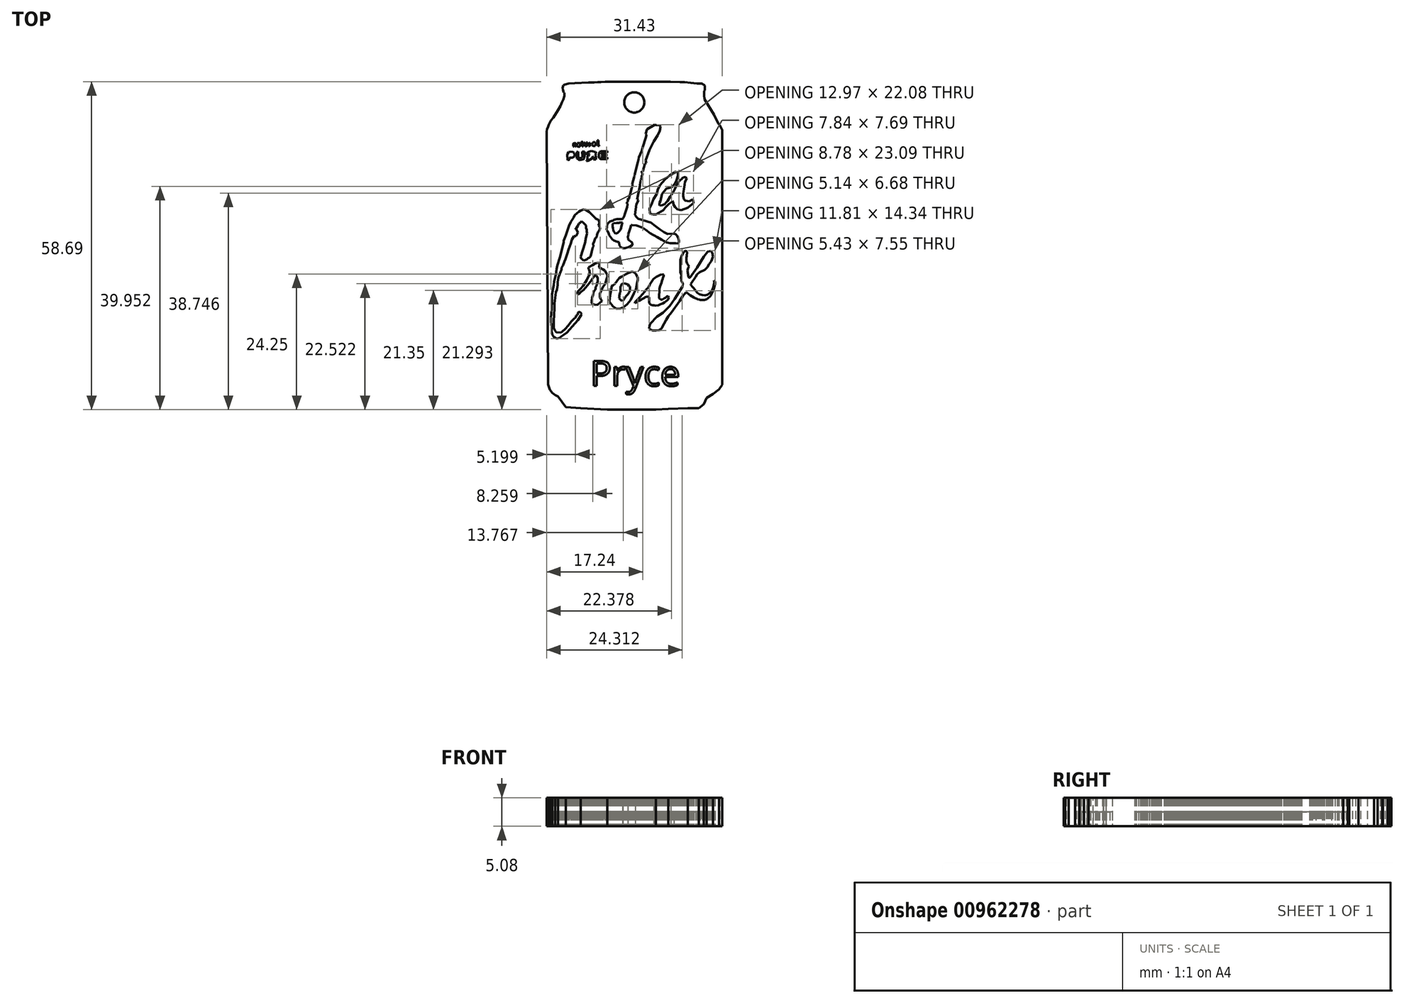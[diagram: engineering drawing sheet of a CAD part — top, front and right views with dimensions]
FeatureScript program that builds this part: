
annotation { "Feature Type Name" : "Feature", "Feature Type Description" : "" }
export const myFeature = defineFeature(function(context is Context, id is Id, definition is map)
    precondition{}
    {
        {
            var Q0;
            Q0=qCreatedBy(makeId("Top.planeOp"),FACE);
            var sketch = newSketch(context, id + "F0", { "sketchPlane" : qUnion([Q0])});
            skLineSegment(sketch, "E0", {"start": v(-26.3, 34.2) * mm, "end": v(-26, -11.02) * mm});
            skLineSegment(sketch, "E1", {"start": v(-26, -11.02) * mm, "end": v(-25.72, -12.03) * mm});
            skLineSegment(sketch, "E2", {"start": v(-25.72, -12.03) * mm, "end": v(-25.25, -12.55) * mm});
            skLineSegment(sketch, "E3", {"start": v(-25.25, -12.55) * mm, "end": v(-24.77, -12.95) * mm});
            skLineSegment(sketch, "E4", {"start": v(-24.77, -12.95) * mm, "end": v(-24.25, -13.22) * mm});
            skLineSegment(sketch, "E5", {"start": v(-24.25, -13.22) * mm, "end": v(-22.83, -15.1) * mm});
            skLineSegment(sketch, "E6", {"start": v(-22.83, -15.1) * mm, "end": v(-20.16, -15.3) * mm});
            skLineSegment(sketch, "E7", {"start": v(-20.16, -15.3) * mm, "end": v(-17.96, -15.41) * mm});
            skLineSegment(sketch, "E8", {"start": v(-17.96, -15.41) * mm, "end": v(-15.42, -15.55) * mm});
            skLineSegment(sketch, "E9", {"start": v(-15.42, -15.55) * mm, "end": v(-12.93, -15.55) * mm});
            skLineSegment(sketch, "E10", {"start": v(-12.93, -15.55) * mm, "end": v(-10.85, -15.55) * mm});
            skLineSegment(sketch, "E11", {"start": v(-10.85, -15.55) * mm, "end": v(-9.02, -15.55) * mm});
            skLineSegment(sketch, "E12", {"start": v(-9.02, -15.55) * mm, "end": v(-6.74, -15.55) * mm});
            skLineSegment(sketch, "E13", {"start": v(-6.74, -15.55) * mm, "end": v(-4.52, -15.41) * mm});
            skLineSegment(sketch, "E14", {"start": v(-4.52, -15.41) * mm, "end": v(-1, -15.27) * mm});
            skLineSegment(sketch, "E15", {"start": v(-1, -15.27) * mm, "end": v(0.95, -15.27) * mm});
            skLineSegment(sketch, "E16", {"start": v(0.95, -15.27) * mm, "end": v(1.88, -14.61) * mm});
            skLineSegment(sketch, "E17", {"start": v(1.88, -14.61) * mm, "end": v(2.35, -13.48) * mm});
            skLineSegment(sketch, "E18", {"start": v(2.35, -13.48) * mm, "end": v(3.5, -12.76) * mm});
            skLineSegment(sketch, "E19", {"start": v(3.5, -12.76) * mm, "end": v(4.6, -11.91) * mm});
            skLineSegment(sketch, "E20", {"start": v(4.6, -11.91) * mm, "end": v(5.13, -11.11) * mm});
            skLineSegment(sketch, "E21", {"start": v(5.13, -11.11) * mm, "end": v(5.13, -10.3) * mm});
            skLineSegment(sketch, "E22", {"start": v(5.13, -10.3) * mm, "end": v(5.13, -6.08) * mm});
            skLineSegment(sketch, "E23", {"start": v(5.13, -6.08) * mm, "end": v(5.13, -5.6) * mm});
            skLineSegment(sketch, "E24", {"start": v(5.13, -5.6) * mm, "end": v(5.13, 0.5) * mm});
            skLineSegment(sketch, "E25", {"start": v(5.13, 0.5) * mm, "end": v(5.13, 34.49) * mm});
            skLineSegment(sketch, "E26", {"start": v(5.13, 34.49) * mm, "end": v(4.7, 35.36) * mm});
            skLineSegment(sketch, "E27", {"start": v(4.7, 35.36) * mm, "end": v(4.48, 35.62) * mm});
            skLineSegment(sketch, "E28", {"start": v(4.48, 35.62) * mm, "end": v(3.68, 37.23) * mm});
            skLineSegment(sketch, "E29", {"start": v(3.68, 37.23) * mm, "end": v(3.07, 38.24) * mm});
            skLineSegment(sketch, "E30", {"start": v(3.07, 38.24) * mm, "end": v(2, 40.03) * mm});
            skLineSegment(sketch, "E31", {"start": v(2, 40.03) * mm, "end": v(1.9, 40.69) * mm});
            skLineSegment(sketch, "E32", {"start": v(1.9, 40.69) * mm, "end": v(1.9, 41.12) * mm});
            skLineSegment(sketch, "E33", {"start": v(1.9, 41.12) * mm, "end": v(1.9, 41.46) * mm});
            skLineSegment(sketch, "E34", {"start": v(1.9, 41.46) * mm, "end": v(2.07, 41.6) * mm});
            skLineSegment(sketch, "E35", {"start": v(2.07, 41.6) * mm, "end": v(2.07, 41.93) * mm});
            skLineSegment(sketch, "E36", {"start": v(2.07, 41.93) * mm, "end": v(2.07, 42.42) * mm});
            skLineSegment(sketch, "E37", {"start": v(2.07, 42.42) * mm, "end": v(1.95, 42.56) * mm});
            skLineSegment(sketch, "E38", {"start": v(1.95, 42.56) * mm, "end": v(1.49, 42.8) * mm});
            skLineSegment(sketch, "E39", {"start": v(1.49, 42.8) * mm, "end": v(0.65, 42.8) * mm});
            skLineSegment(sketch, "E40", {"start": v(0.65, 42.8) * mm, "end": v(-0.46, 42.95) * mm});
            skLineSegment(sketch, "E41", {"start": v(-0.46, 42.95) * mm, "end": v(-1.54, 43.05) * mm});
            skLineSegment(sketch, "E42", {"start": v(-1.54, 43.05) * mm, "end": v(-2.4, 43.05) * mm});
            skLineSegment(sketch, "E43", {"start": v(-2.4, 43.05) * mm, "end": v(-4.13, 43.14) * mm});
            skLineSegment(sketch, "E44", {"start": v(-4.13, 43.14) * mm, "end": v(-5.15, 43.14) * mm});
            skLineSegment(sketch, "E45", {"start": v(-5.15, 43.14) * mm, "end": v(-6.54, 43.14) * mm});
            skLineSegment(sketch, "E46", {"start": v(-6.54, 43.14) * mm, "end": v(-8.61, 43.14) * mm});
            skLineSegment(sketch, "E47", {"start": v(-8.61, 43.14) * mm, "end": v(-9.4, 43.14) * mm});
            skLineSegment(sketch, "E48", {"start": v(-9.4, 43.14) * mm, "end": v(-10.07, 43.14) * mm});
            skLineSegment(sketch, "E49", {"start": v(-10.07, 43.14) * mm, "end": v(-11.08, 43.14) * mm});
            skLineSegment(sketch, "E50", {"start": v(-11.08, 43.14) * mm, "end": v(-13.23, 43.14) * mm});
            skLineSegment(sketch, "E51", {"start": v(-13.23, 43.14) * mm, "end": v(-14.73, 43.14) * mm});
            skLineSegment(sketch, "E52", {"start": v(-14.73, 43.14) * mm, "end": v(-15.8, 43.14) * mm});
            skLineSegment(sketch, "E53", {"start": v(-15.8, 43.14) * mm, "end": v(-16.56, 43.05) * mm});
            skLineSegment(sketch, "E54", {"start": v(-16.56, 43.05) * mm, "end": v(-17.14, 43.05) * mm});
            skLineSegment(sketch, "E55", {"start": v(-17.14, 43.05) * mm, "end": v(-17.78, 42.99) * mm});
            skLineSegment(sketch, "E56", {"start": v(-17.78, 42.99) * mm, "end": v(-18.77, 42.99) * mm});
            skLineSegment(sketch, "E57", {"start": v(-18.77, 42.99) * mm, "end": v(-20.2, 42.93) * mm});
            skLineSegment(sketch, "E58", {"start": v(-20.2, 42.93) * mm, "end": v(-21.23, 42.88) * mm});
            skLineSegment(sketch, "E59", {"start": v(-21.23, 42.88) * mm, "end": v(-22.32, 42.8) * mm});
            skLineSegment(sketch, "E60", {"start": v(-22.32, 42.8) * mm, "end": v(-23.06, 42.6) * mm});
            skLineSegment(sketch, "E61", {"start": v(-23.06, 42.6) * mm, "end": v(-23.3, 42.46) * mm});
            skLineSegment(sketch, "E62", {"start": v(-23.3, 42.46) * mm, "end": v(-23.4, 42.01) * mm});
            skLineSegment(sketch, "E63", {"start": v(-23.4, 42.01) * mm, "end": v(-23.38, 41.66) * mm});
            skLineSegment(sketch, "E64", {"start": v(-23.38, 41.66) * mm, "end": v(-23.2, 41.21) * mm});
            skLineSegment(sketch, "E65", {"start": v(-23.2, 41.21) * mm, "end": v(-23.12, 41.12) * mm});
            skLineSegment(sketch, "E66", {"start": v(-23.12, 41.12) * mm, "end": v(-23.12, 40.57) * mm});
            skLineSegment(sketch, "E67", {"start": v(-23.12, 40.57) * mm, "end": v(-23.3, 39.97) * mm});
            skLineSegment(sketch, "E68", {"start": v(-23.3, 39.97) * mm, "end": v(-23.54, 39.42) * mm});
            skLineSegment(sketch, "E69", {"start": v(-23.54, 39.42) * mm, "end": v(-23.8, 38.82) * mm});
            skLineSegment(sketch, "E70", {"start": v(-23.8, 38.82) * mm, "end": v(-24.26, 38.06) * mm});
            skLineSegment(sketch, "E71", {"start": v(-24.26, 38.06) * mm, "end": v(-24.64, 37.44) * mm});
            skLineSegment(sketch, "E72", {"start": v(-24.64, 37.44) * mm, "end": v(-25.09, 36.7) * mm});
            skLineSegment(sketch, "E73", {"start": v(-25.09, 36.7) * mm, "end": v(-25.5, 36.19) * mm});
            skLineSegment(sketch, "E74", {"start": v(-25.5, 36.19) * mm, "end": v(-25.88, 35.44) * mm});
            skLineSegment(sketch, "E75", {"start": v(-25.88, 35.44) * mm, "end": v(-26.04, 35.02) * mm});
            skLineSegment(sketch, "E76", {"start": v(-26.04, 35.02) * mm, "end": v(-26.18, 34.6) * mm});
            skLineSegment(sketch, "E77", {"start": v(-26.18, 34.6) * mm, "end": v(-26.3, 34.2) * mm});
            skLineSegment(sketch, "E78", {"start": v(-8.56, 33.78) * mm, "end": v(-8.31, 34.6) * mm});
            skLineSegment(sketch, "E79", {"start": v(-8.31, 34.6) * mm, "end": v(-6.9, 35.44) * mm});
            skLineSegment(sketch, "E80", {"start": v(-6.9, 35.44) * mm, "end": v(-6.71, 35.38) * mm});
            skLineSegment(sketch, "E81", {"start": v(-6.71, 35.38) * mm, "end": v(-6.17, 35.32) * mm});
            skLineSegment(sketch, "E82", {"start": v(-6.17, 35.32) * mm, "end": v(-6.04, 35.32) * mm});
            skLineSegment(sketch, "E83", {"start": v(-6.04, 35.32) * mm, "end": v(-5.88, 35.05) * mm});
            skLineSegment(sketch, "E84", {"start": v(-5.88, 35.05) * mm, "end": v(-6, 34.33) * mm});
            skLineSegment(sketch, "E85", {"start": v(-6, 34.33) * mm, "end": v(-6.2, 33.97) * mm});
            skLineSegment(sketch, "E86", {"start": v(-6.2, 33.97) * mm, "end": v(-6.4, 33.55) * mm});
            skLineSegment(sketch, "E87", {"start": v(-6.4, 33.55) * mm, "end": v(-7.09, 32.44) * mm});
            skLineSegment(sketch, "E88", {"start": v(-7.09, 32.44) * mm, "end": v(-7.84, 30.96) * mm});
            skLineSegment(sketch, "E89", {"start": v(-7.84, 30.96) * mm, "end": v(-8.54, 29) * mm});
            skLineSegment(sketch, "E90", {"start": v(-8.54, 29) * mm, "end": v(-8.44, 28.6) * mm});
            skLineSegment(sketch, "E91", {"start": v(-8.44, 28.6) * mm, "end": v(-8.66, 28.48) * mm});
            skLineSegment(sketch, "E92", {"start": v(-8.66, 28.48) * mm, "end": v(-9.1, 27.04) * mm});
            skLineSegment(sketch, "E93", {"start": v(-9.1, 27.04) * mm, "end": v(-9.26, 27.1) * mm});
            skLineSegment(sketch, "E94", {"start": v(-9.26, 27.1) * mm, "end": v(-9.26, 26.85) * mm});
            skLineSegment(sketch, "E95", {"start": v(-9.26, 26.85) * mm, "end": v(-9.1, 26.7) * mm});
            skLineSegment(sketch, "E96", {"start": v(-9.1, 26.7) * mm, "end": v(-9.17, 26.27) * mm});
            skLineSegment(sketch, "E97", {"start": v(-9.17, 26.27) * mm, "end": v(-9.28, 26.17) * mm});
            skLineSegment(sketch, "E98", {"start": v(-9.28, 26.17) * mm, "end": v(-9.38, 26.09) * mm});
            skLineSegment(sketch, "E99", {"start": v(-9.38, 26.09) * mm, "end": v(-9.28, 25.93) * mm});
            skLineSegment(sketch, "E100", {"start": v(-9.28, 25.93) * mm, "end": v(-9.42, 25.66) * mm});
            skLineSegment(sketch, "E101", {"start": v(-9.42, 25.66) * mm, "end": v(-9.41, 25.44) * mm});
            skLineSegment(sketch, "E102", {"start": v(-9.41, 25.44) * mm, "end": v(-9.5, 25.26) * mm});
            skLineSegment(sketch, "E103", {"start": v(-9.5, 25.26) * mm, "end": v(-9.58, 24.53) * mm});
            skLineSegment(sketch, "E104", {"start": v(-9.58, 24.53) * mm, "end": v(-10.07, 22) * mm});
            skLineSegment(sketch, "E105", {"start": v(-10.07, 22) * mm, "end": v(-9.85, 21.9) * mm});
            skLineSegment(sketch, "E106", {"start": v(-9.85, 21.9) * mm, "end": v(-10.2, 21.19) * mm});
            skLineSegment(sketch, "E107", {"start": v(-10.2, 21.19) * mm, "end": v(-10.47, 19.31) * mm});
            skLineSegment(sketch, "E108", {"start": v(-10.47, 19.31) * mm, "end": v(-10.23, 18.91) * mm});
            skLineSegment(sketch, "E109", {"start": v(-10.23, 18.91) * mm, "end": v(-9.88, 18.6) * mm});
            skLineSegment(sketch, "E110", {"start": v(-9.88, 18.6) * mm, "end": v(-8.89, 18.3) * mm});
            skLineSegment(sketch, "E111", {"start": v(-8.89, 18.3) * mm, "end": v(-7.6, 17.92) * mm});
            skLineSegment(sketch, "E112", {"start": v(-7.6, 17.92) * mm, "end": v(-6.76, 17.27) * mm});
            skLineSegment(sketch, "E113", {"start": v(-6.76, 17.27) * mm, "end": v(-6.05, 16.68) * mm});
            skLineSegment(sketch, "E114", {"start": v(-6.05, 16.68) * mm, "end": v(-5.26, 16.2) * mm});
            skLineSegment(sketch, "E115", {"start": v(-5.26, 16.2) * mm, "end": v(-4.62, 15.88) * mm});
            skLineSegment(sketch, "E116", {"start": v(-4.62, 15.88) * mm, "end": v(-3.46, 15.93) * mm});
            skLineSegment(sketch, "E117", {"start": v(-3.46, 15.93) * mm, "end": v(-3.15, 15.84) * mm});
            skLineSegment(sketch, "E118", {"start": v(-3.15, 15.84) * mm, "end": v(-2.98, 15.64) * mm});
            skLineSegment(sketch, "E119", {"start": v(-2.98, 15.64) * mm, "end": v(-2.71, 15.19) * mm});
            skLineSegment(sketch, "E120", {"start": v(-2.71, 15.19) * mm, "end": v(-2.58, 14.7) * mm});
            skLineSegment(sketch, "E121", {"start": v(-2.58, 14.7) * mm, "end": v(-2.58, 14.35) * mm});
            skLineSegment(sketch, "E122", {"start": v(-2.58, 14.35) * mm, "end": v(-2.8, 14.17) * mm});
            skLineSegment(sketch, "E123", {"start": v(-2.8, 14.17) * mm, "end": v(-3.17, 14.22) * mm});
            skLineSegment(sketch, "E124", {"start": v(-3.17, 14.22) * mm, "end": v(-4.17, 14.22) * mm});
            skLineSegment(sketch, "E125", {"start": v(-4.17, 14.22) * mm, "end": v(-4.73, 14.37) * mm});
            skLineSegment(sketch, "E126", {"start": v(-4.73, 14.37) * mm, "end": v(-5.24, 14.58) * mm});
            skLineSegment(sketch, "E127", {"start": v(-5.24, 14.58) * mm, "end": v(-5.73, 14.88) * mm});
            skLineSegment(sketch, "E128", {"start": v(-5.73, 14.88) * mm, "end": v(-6.46, 15.32) * mm});
            skLineSegment(sketch, "E129", {"start": v(-6.46, 15.32) * mm, "end": v(-7.75, 15.99) * mm});
            skLineSegment(sketch, "E130", {"start": v(-7.75, 15.99) * mm, "end": v(-8.59, 16.62) * mm});
            skLineSegment(sketch, "E131", {"start": v(-8.59, 16.62) * mm, "end": v(-9.13, 17) * mm});
            skLineSegment(sketch, "E132", {"start": v(-9.13, 17) * mm, "end": v(-10.21, 17.38) * mm});
            skLineSegment(sketch, "E133", {"start": v(-10.21, 17.38) * mm, "end": v(-11, 17.46) * mm});
            skLineSegment(sketch, "E134", {"start": v(-11, 17.46) * mm, "end": v(-11.19, 17.46) * mm});
            skLineSegment(sketch, "E135", {"start": v(-11.19, 17.46) * mm, "end": v(-11.24, 17.12) * mm});
            skLineSegment(sketch, "E136", {"start": v(-11.24, 17.12) * mm, "end": v(-11.52, 16.2) * mm});
            skLineSegment(sketch, "E137", {"start": v(-11.52, 16.2) * mm, "end": v(-11.7, 15.86) * mm});
            skLineSegment(sketch, "E138", {"start": v(-11.7, 15.86) * mm, "end": v(-11.6, 15.68) * mm});
            skLineSegment(sketch, "E139", {"start": v(-11.6, 15.68) * mm, "end": v(-11.74, 15.46) * mm});
            skLineSegment(sketch, "E140", {"start": v(-11.74, 15.46) * mm, "end": v(-11.68, 14.86) * mm});
            skLineSegment(sketch, "E141", {"start": v(-11.68, 14.86) * mm, "end": v(-11, 14.37) * mm});
            skLineSegment(sketch, "E142", {"start": v(-11, 14.37) * mm, "end": v(-10.89, 13.9) * mm});
            skLineSegment(sketch, "E143", {"start": v(-10.89, 13.9) * mm, "end": v(-11.42, 13.57) * mm});
            skLineSegment(sketch, "E144", {"start": v(-11.42, 13.57) * mm, "end": v(-12.25, 13.36) * mm});
            skLineSegment(sketch, "E145", {"start": v(-12.25, 13.36) * mm, "end": v(-12.65, 13.36) * mm});
            skLineSegment(sketch, "E146", {"start": v(-12.65, 13.36) * mm, "end": v(-13.06, 13.57) * mm});
            skLineSegment(sketch, "E147", {"start": v(-13.06, 13.57) * mm, "end": v(-13.23, 13.86) * mm});
            skLineSegment(sketch, "E148", {"start": v(-13.23, 13.86) * mm, "end": v(-13.34, 14.43) * mm});
            skLineSegment(sketch, "E149", {"start": v(-13.34, 14.43) * mm, "end": v(-13.8, 14.57) * mm});
            skLineSegment(sketch, "E150", {"start": v(-13.8, 14.57) * mm, "end": v(-14.25, 14.75) * mm});
            skLineSegment(sketch, "E151", {"start": v(-14.25, 14.75) * mm, "end": v(-14.5, 14.93) * mm});
            skLineSegment(sketch, "E152", {"start": v(-14.5, 14.93) * mm, "end": v(-15.08, 15.7) * mm});
            skLineSegment(sketch, "E153", {"start": v(-15.08, 15.7) * mm, "end": v(-15.13, 15.98) * mm});
            skLineSegment(sketch, "E154", {"start": v(-15.13, 15.98) * mm, "end": v(-15.4, 16.43) * mm});
            skLineSegment(sketch, "E155", {"start": v(-15.4, 16.43) * mm, "end": v(-15.54, 16.6) * mm});
            skLineSegment(sketch, "E156", {"start": v(-15.54, 16.6) * mm, "end": v(-15.49, 17.15) * mm});
            skLineSegment(sketch, "E157", {"start": v(-15.49, 17.15) * mm, "end": v(-15.4, 17.64) * mm});
            skLineSegment(sketch, "E158", {"start": v(-15.4, 17.64) * mm, "end": v(-14.99, 18.07) * mm});
            skLineSegment(sketch, "E159", {"start": v(-14.99, 18.07) * mm, "end": v(-14.61, 18.25) * mm});
            skLineSegment(sketch, "E160", {"start": v(-14.61, 18.25) * mm, "end": v(-14.41, 18.25) * mm});
            skLineSegment(sketch, "E161", {"start": v(-14.41, 18.25) * mm, "end": v(-14.22, 18.42) * mm});
            skLineSegment(sketch, "E162", {"start": v(-14.22, 18.42) * mm, "end": v(-13.67, 18.52) * mm});
            skLineSegment(sketch, "E163", {"start": v(-13.67, 18.52) * mm, "end": v(-13.22, 18.55) * mm});
            skLineSegment(sketch, "E164", {"start": v(-13.22, 18.55) * mm, "end": v(-12.9, 18.54) * mm});
            skLineSegment(sketch, "E165", {"start": v(-12.9, 18.54) * mm, "end": v(-12.71, 18.54) * mm});
            skLineSegment(sketch, "E166", {"start": v(-12.71, 18.54) * mm, "end": v(-12.54, 18.71) * mm});
            skLineSegment(sketch, "E167", {"start": v(-12.54, 18.71) * mm, "end": v(-12.46, 18.87) * mm});
            skLineSegment(sketch, "E168", {"start": v(-12.46, 18.87) * mm, "end": v(-12.34, 19.12) * mm});
            skLineSegment(sketch, "E169", {"start": v(-12.34, 19.12) * mm, "end": v(-12.27, 19.39) * mm});
            skLineSegment(sketch, "E170", {"start": v(-12.27, 19.39) * mm, "end": v(-11.87, 20.73) * mm});
            skLineSegment(sketch, "E171", {"start": v(-11.87, 20.73) * mm, "end": v(-11.78, 21.13) * mm});
            skLineSegment(sketch, "E172", {"start": v(-11.78, 21.13) * mm, "end": v(-11.8, 21.25) * mm});
            skLineSegment(sketch, "E173", {"start": v(-11.8, 21.25) * mm, "end": v(-11.92, 21.27) * mm});
            skLineSegment(sketch, "E174", {"start": v(-11.92, 21.27) * mm, "end": v(-11.84, 21.57) * mm});
            skLineSegment(sketch, "E175", {"start": v(-11.84, 21.57) * mm, "end": v(-11.71, 21.67) * mm});
            skLineSegment(sketch, "E176", {"start": v(-11.71, 21.67) * mm, "end": v(-11.73, 21.81) * mm});
            skLineSegment(sketch, "E177", {"start": v(-11.73, 21.81) * mm, "end": v(-11.84, 21.94) * mm});
            skLineSegment(sketch, "E178", {"start": v(-11.84, 21.94) * mm, "end": v(-11.55, 22.17) * mm});
            skLineSegment(sketch, "E179", {"start": v(-11.55, 22.17) * mm, "end": v(-11.47, 22.45) * mm});
            skLineSegment(sketch, "E180", {"start": v(-11.47, 22.45) * mm, "end": v(-11.4, 22.74) * mm});
            skLineSegment(sketch, "E181", {"start": v(-11.4, 22.74) * mm, "end": v(-11.33, 22.93) * mm});
            skLineSegment(sketch, "E182", {"start": v(-11.33, 22.93) * mm, "end": v(-11.3, 23.18) * mm});
            skLineSegment(sketch, "E183", {"start": v(-11.3, 23.18) * mm, "end": v(-11.19, 23.64) * mm});
            skLineSegment(sketch, "E184", {"start": v(-11.19, 23.64) * mm, "end": v(-11.06, 24.12) * mm});
            skLineSegment(sketch, "E185", {"start": v(-11.06, 24.12) * mm, "end": v(-10.9, 24.3) * mm});
            skLineSegment(sketch, "E186", {"start": v(-10.9, 24.3) * mm, "end": v(-10.91, 24.62) * mm});
            skLineSegment(sketch, "E187", {"start": v(-10.91, 24.62) * mm, "end": v(-10.96, 24.76) * mm});
            skLineSegment(sketch, "E188", {"start": v(-10.96, 24.76) * mm, "end": v(-10.88, 25.05) * mm});
            skLineSegment(sketch, "E189", {"start": v(-10.88, 25.05) * mm, "end": v(-10.77, 25.5) * mm});
            skLineSegment(sketch, "E190", {"start": v(-10.77, 25.5) * mm, "end": v(-10.64, 25.93) * mm});
            skLineSegment(sketch, "E191", {"start": v(-10.64, 25.93) * mm, "end": v(-10.58, 26.12) * mm});
            skLineSegment(sketch, "E192", {"start": v(-10.58, 26.12) * mm, "end": v(-10.65, 26.23) * mm});
            skLineSegment(sketch, "E193", {"start": v(-10.65, 26.23) * mm, "end": v(-10.5, 26.37) * mm});
            skLineSegment(sketch, "E194", {"start": v(-10.5, 26.37) * mm, "end": v(-10.5, 26.49) * mm});
            skLineSegment(sketch, "E195", {"start": v(-10.5, 26.49) * mm, "end": v(-10.19, 27.69) * mm});
            skLineSegment(sketch, "E196", {"start": v(-10.19, 27.69) * mm, "end": v(-9.93, 28.71) * mm});
            skLineSegment(sketch, "E197", {"start": v(-9.93, 28.71) * mm, "end": v(-9.82, 29.22) * mm});
            skLineSegment(sketch, "E198", {"start": v(-9.82, 29.22) * mm, "end": v(-9.74, 29.6) * mm});
            skLineSegment(sketch, "E199", {"start": v(-9.74, 29.6) * mm, "end": v(-9.28, 30.74) * mm});
            skLineSegment(sketch, "E200", {"start": v(-9.28, 30.74) * mm, "end": v(-9.14, 31.15) * mm});
            skLineSegment(sketch, "E201", {"start": v(-9.14, 31.15) * mm, "end": v(-9.05, 31.45) * mm});
            skLineSegment(sketch, "E202", {"start": v(-9.05, 31.45) * mm, "end": v(-8.57, 33.03) * mm});
            skLineSegment(sketch, "E203", {"start": v(-8.57, 33.03) * mm, "end": v(-8.46, 33.46) * mm});
            skLineSegment(sketch, "E204", {"start": v(-8.46, 33.46) * mm, "end": v(-8.46, 33.64) * mm});
            skLineSegment(sketch, "E205", {"start": v(-8.46, 33.64) * mm, "end": v(-8.56, 33.78) * mm});
            skLineSegment(sketch, "E206", {"start": v(-14.22, 16.25) * mm, "end": v(-14.02, 16) * mm});
            skLineSegment(sketch, "E207", {"start": v(-14.02, 16) * mm, "end": v(-13.93, 15.96) * mm});
            skLineSegment(sketch, "E208", {"start": v(-13.93, 15.96) * mm, "end": v(-13.74, 16.02) * mm});
            skLineSegment(sketch, "E209", {"start": v(-13.74, 16.02) * mm, "end": v(-13.58, 16.1) * mm});
            skLineSegment(sketch, "E210", {"start": v(-13.58, 16.1) * mm, "end": v(-13.3, 16.3) * mm});
            skLineSegment(sketch, "E211", {"start": v(-13.3, 16.3) * mm, "end": v(-13, 16.7) * mm});
            skLineSegment(sketch, "E212", {"start": v(-13, 16.7) * mm, "end": v(-12.85, 17.3) * mm});
            skLineSegment(sketch, "E213", {"start": v(-12.85, 17.3) * mm, "end": v(-12.76, 17.79) * mm});
            skLineSegment(sketch, "E214", {"start": v(-12.76, 17.79) * mm, "end": v(-12.77, 17.89) * mm});
            skLineSegment(sketch, "E215", {"start": v(-12.77, 17.89) * mm, "end": v(-13.04, 17.96) * mm});
            skLineSegment(sketch, "E216", {"start": v(-13.04, 17.96) * mm, "end": v(-13.3, 17.86) * mm});
            skLineSegment(sketch, "E217", {"start": v(-13.3, 17.86) * mm, "end": v(-13.77, 17.82) * mm});
            skLineSegment(sketch, "E218", {"start": v(-13.77, 17.82) * mm, "end": v(-14.25, 17.76) * mm});
            skLineSegment(sketch, "E219", {"start": v(-14.25, 17.76) * mm, "end": v(-14.48, 17.67) * mm});
            skLineSegment(sketch, "E220", {"start": v(-14.48, 17.67) * mm, "end": v(-14.46, 17.24) * mm});
            skLineSegment(sketch, "E221", {"start": v(-14.46, 17.24) * mm, "end": v(-14.38, 16.86) * mm});
            skLineSegment(sketch, "E222", {"start": v(-14.38, 16.86) * mm, "end": v(-14.3, 16.5) * mm});
            skLineSegment(sketch, "E223", {"start": v(-14.3, 16.5) * mm, "end": v(-14.22, 16.25) * mm});
            skLineSegment(sketch, "E224", {"start": v(-3.1, 27.04) * mm, "end": v(-4.22, 26.37) * mm});
            skLineSegment(sketch, "E225", {"start": v(-4.22, 26.37) * mm, "end": v(-5.15, 25.6) * mm});
            skLineSegment(sketch, "E226", {"start": v(-5.15, 25.6) * mm, "end": v(-5.96, 24.64) * mm});
            skLineSegment(sketch, "E227", {"start": v(-5.96, 24.64) * mm, "end": v(-6.32, 23.94) * mm});
            skLineSegment(sketch, "E228", {"start": v(-6.32, 23.94) * mm, "end": v(-6.6, 23) * mm});
            skLineSegment(sketch, "E229", {"start": v(-6.6, 23) * mm, "end": v(-7.16, 22.1) * mm});
            skLineSegment(sketch, "E230", {"start": v(-7.16, 22.1) * mm, "end": v(-7.47, 21.19) * mm});
            skLineSegment(sketch, "E231", {"start": v(-7.47, 21.19) * mm, "end": v(-7.84, 20.47) * mm});
            skLineSegment(sketch, "E232", {"start": v(-7.84, 20.47) * mm, "end": v(-7.8, 19.58) * mm});
            skLineSegment(sketch, "E233", {"start": v(-7.8, 19.58) * mm, "end": v(-7.5, 19.4) * mm});
            skLineSegment(sketch, "E234", {"start": v(-7.5, 19.4) * mm, "end": v(-7.17, 19.35) * mm});
            skLineSegment(sketch, "E235", {"start": v(-7.17, 19.35) * mm, "end": v(-6.7, 19.36) * mm});
            skLineSegment(sketch, "E236", {"start": v(-6.7, 19.36) * mm, "end": v(-5.37, 20.15) * mm});
            skLineSegment(sketch, "E237", {"start": v(-5.37, 20.15) * mm, "end": v(-4.97, 20.63) * mm});
            skLineSegment(sketch, "E238", {"start": v(-4.97, 20.63) * mm, "end": v(-4.38, 21.3) * mm});
            skLineSegment(sketch, "E239", {"start": v(-4.38, 21.3) * mm, "end": v(-3.82, 21.68) * mm});
            skLineSegment(sketch, "E240", {"start": v(-3.82, 21.68) * mm, "end": v(-3.75, 21.8) * mm});
            skLineSegment(sketch, "E241", {"start": v(-3.75, 21.8) * mm, "end": v(-3.6, 21.6) * mm});
            skLineSegment(sketch, "E242", {"start": v(-3.6, 21.6) * mm, "end": v(-3.6, 21.21) * mm});
            skLineSegment(sketch, "E243", {"start": v(-3.6, 21.21) * mm, "end": v(-3.3, 20.7) * mm});
            skLineSegment(sketch, "E244", {"start": v(-3.3, 20.7) * mm, "end": v(-2.9, 20.3) * mm});
            skLineSegment(sketch, "E245", {"start": v(-2.9, 20.3) * mm, "end": v(-2.2, 20.14) * mm});
            skLineSegment(sketch, "E246", {"start": v(-2.2, 20.14) * mm, "end": v(-1, 20.56) * mm});
            skLineSegment(sketch, "E247", {"start": v(-1, 20.56) * mm, "end": v(-0.38, 21.08) * mm});
            skLineSegment(sketch, "E248", {"start": v(-0.38, 21.08) * mm, "end": v(0, 21.39) * mm});
            skLineSegment(sketch, "E249", {"start": v(0, 21.39) * mm, "end": v(-0.03, 21.98) * mm});
            skLineSegment(sketch, "E250", {"start": v(-0.03, 21.98) * mm, "end": v(-0.2, 22.03) * mm});
            skLineSegment(sketch, "E251", {"start": v(-0.2, 22.03) * mm, "end": v(-0.73, 21.72) * mm});
            skLineSegment(sketch, "E252", {"start": v(-0.73, 21.72) * mm, "end": v(-1.46, 21.85) * mm});
            skLineSegment(sketch, "E253", {"start": v(-1.46, 21.85) * mm, "end": v(-1.72, 22.07) * mm});
            skLineSegment(sketch, "E254", {"start": v(-1.72, 22.07) * mm, "end": v(-1.77, 22.37) * mm});
            skLineSegment(sketch, "E255", {"start": v(-1.77, 22.37) * mm, "end": v(-1.84, 22.67) * mm});
            skLineSegment(sketch, "E256", {"start": v(-1.84, 22.67) * mm, "end": v(-1.8, 23.15) * mm});
            skLineSegment(sketch, "E257", {"start": v(-1.8, 23.15) * mm, "end": v(-1.67, 23.86) * mm});
            skLineSegment(sketch, "E258", {"start": v(-1.67, 23.86) * mm, "end": v(-1.55, 24.7) * mm});
            skLineSegment(sketch, "E259", {"start": v(-1.55, 24.7) * mm, "end": v(-1.49, 25.21) * mm});
            skLineSegment(sketch, "E260", {"start": v(-1.49, 25.21) * mm, "end": v(-1.25, 25.64) * mm});
            skLineSegment(sketch, "E261", {"start": v(-1.25, 25.64) * mm, "end": v(-1.18, 25.83) * mm});
            skLineSegment(sketch, "E262", {"start": v(-1.18, 25.83) * mm, "end": v(-1.36, 26.02) * mm});
            skLineSegment(sketch, "E263", {"start": v(-1.36, 26.02) * mm, "end": v(-1.65, 26.03) * mm});
            skLineSegment(sketch, "E264", {"start": v(-1.65, 26.03) * mm, "end": v(-1.97, 25.9) * mm});
            skLineSegment(sketch, "E265", {"start": v(-1.97, 25.9) * mm, "end": v(-2.08, 25.73) * mm});
            skLineSegment(sketch, "E266", {"start": v(-2.08, 25.73) * mm, "end": v(-2.32, 25.52) * mm});
            skLineSegment(sketch, "E267", {"start": v(-2.32, 25.52) * mm, "end": v(-2.5, 25.35) * mm});
            skLineSegment(sketch, "E268", {"start": v(-2.5, 25.35) * mm, "end": v(-2.64, 25.15) * mm});
            skLineSegment(sketch, "E269", {"start": v(-2.64, 25.15) * mm, "end": v(-2.8, 25.04) * mm});
            skLineSegment(sketch, "E270", {"start": v(-2.8, 25.04) * mm, "end": v(-2.92, 24.74) * mm});
            skLineSegment(sketch, "E271", {"start": v(-2.92, 24.74) * mm, "end": v(-3.22, 24.21) * mm});
            skLineSegment(sketch, "E272", {"start": v(-3.22, 24.21) * mm, "end": v(-3.31, 23.99) * mm});
            skLineSegment(sketch, "E273", {"start": v(-3.31, 23.99) * mm, "end": v(-3.35, 23.9) * mm});
            skLineSegment(sketch, "E274", {"start": v(-3.35, 23.9) * mm, "end": v(-3.63, 23.35) * mm});
            skLineSegment(sketch, "E275", {"start": v(-3.63, 23.35) * mm, "end": v(-4.18, 22.57) * mm});
            skLineSegment(sketch, "E276", {"start": v(-4.18, 22.57) * mm, "end": v(-4.65, 21.8) * mm});
            skLineSegment(sketch, "E277", {"start": v(-4.65, 21.8) * mm, "end": v(-4.94, 21.48) * mm});
            skLineSegment(sketch, "E278", {"start": v(-4.94, 21.48) * mm, "end": v(-5.15, 21.23) * mm});
            skLineSegment(sketch, "E279", {"start": v(-5.15, 21.23) * mm, "end": v(-5.63, 21) * mm});
            skLineSegment(sketch, "E280", {"start": v(-5.63, 21) * mm, "end": v(-6.01, 20.96) * mm});
            skLineSegment(sketch, "E281", {"start": v(-6.01, 20.96) * mm, "end": v(-6.07, 21.17) * mm});
            skLineSegment(sketch, "E282", {"start": v(-6.07, 21.17) * mm, "end": v(-6.1, 21.48) * mm});
            skLineSegment(sketch, "E283", {"start": v(-6.1, 21.48) * mm, "end": v(-5.91, 21.79) * mm});
            skLineSegment(sketch, "E284", {"start": v(-5.91, 21.79) * mm, "end": v(-5.6, 22.98) * mm});
            skLineSegment(sketch, "E285", {"start": v(-5.6, 22.98) * mm, "end": v(-5.31, 23.45) * mm});
            skLineSegment(sketch, "E286", {"start": v(-5.31, 23.45) * mm, "end": v(-4.84, 24.03) * mm});
            skLineSegment(sketch, "E287", {"start": v(-4.84, 24.03) * mm, "end": v(-4.32, 24.12) * mm});
            skLineSegment(sketch, "E288", {"start": v(-4.32, 24.12) * mm, "end": v(-3.8, 24.3) * mm});
            skLineSegment(sketch, "E289", {"start": v(-3.8, 24.3) * mm, "end": v(-3.27, 24.9) * mm});
            skLineSegment(sketch, "E290", {"start": v(-3.27, 24.9) * mm, "end": v(-3.04, 25.47) * mm});
            skLineSegment(sketch, "E291", {"start": v(-3.04, 25.47) * mm, "end": v(-2.8, 26.26) * mm});
            skLineSegment(sketch, "E292", {"start": v(-2.8, 26.26) * mm, "end": v(-2.77, 26.6) * mm});
            skLineSegment(sketch, "E293", {"start": v(-2.77, 26.6) * mm, "end": v(-2.79, 26.75) * mm});
            skLineSegment(sketch, "E294", {"start": v(-2.79, 26.75) * mm, "end": v(-2.93, 26.92) * mm});
            skLineSegment(sketch, "E295", {"start": v(-2.93, 26.92) * mm, "end": v(-3.1, 27.04) * mm});
            skLineSegment(sketch, "E296", {"start": v(-20.2, 17.92) * mm, "end": v(-20.03, 18.13) * mm});
            skLineSegment(sketch, "E297", {"start": v(-20.03, 18.13) * mm, "end": v(-19.74, 17.92) * mm});
            skLineSegment(sketch, "E298", {"start": v(-19.74, 17.92) * mm, "end": v(-19.39, 17.57) * mm});
            skLineSegment(sketch, "E299", {"start": v(-19.39, 17.57) * mm, "end": v(-19.2, 17.4) * mm});
            skLineSegment(sketch, "E300", {"start": v(-19.2, 17.4) * mm, "end": v(-19.22, 16.94) * mm});
            skLineSegment(sketch, "E301", {"start": v(-19.22, 16.94) * mm, "end": v(-19.12, 16.64) * mm});
            skLineSegment(sketch, "E302", {"start": v(-19.12, 16.64) * mm, "end": v(-19.1, 16.31) * mm});
            skLineSegment(sketch, "E303", {"start": v(-19.1, 16.31) * mm, "end": v(-19.04, 16.03) * mm});
            skLineSegment(sketch, "E304", {"start": v(-19.04, 16.03) * mm, "end": v(-19.07, 15.73) * mm});
            skLineSegment(sketch, "E305", {"start": v(-19.07, 15.73) * mm, "end": v(-19.23, 15.33) * mm});
            skLineSegment(sketch, "E306", {"start": v(-19.23, 15.33) * mm, "end": v(-19.43, 14.25) * mm});
            skLineSegment(sketch, "E307", {"start": v(-19.43, 14.25) * mm, "end": v(-20.16, 11.8) * mm});
            skLineSegment(sketch, "E308", {"start": v(-20.16, 11.8) * mm, "end": v(-20.1, 11.48) * mm});
            skLineSegment(sketch, "E309", {"start": v(-20.1, 11.48) * mm, "end": v(-19.93, 11.34) * mm});
            skLineSegment(sketch, "E310", {"start": v(-19.93, 11.34) * mm, "end": v(-19.67, 11.13) * mm});
            skLineSegment(sketch, "E311", {"start": v(-19.67, 11.13) * mm, "end": v(-19.32, 11.21) * mm});
            skLineSegment(sketch, "E312", {"start": v(-19.32, 11.21) * mm, "end": v(-19.04, 11.36) * mm});
            skLineSegment(sketch, "E313", {"start": v(-19.04, 11.36) * mm, "end": v(-18.87, 11.55) * mm});
            skLineSegment(sketch, "E314", {"start": v(-18.87, 11.55) * mm, "end": v(-18.65, 11.62) * mm});
            skLineSegment(sketch, "E315", {"start": v(-18.65, 11.62) * mm, "end": v(-18.38, 11.9) * mm});
            skLineSegment(sketch, "E316", {"start": v(-18.38, 11.9) * mm, "end": v(-18.2, 12.73) * mm});
            skLineSegment(sketch, "E317", {"start": v(-18.2, 12.73) * mm, "end": v(-18, 13.45) * mm});
            skLineSegment(sketch, "E318", {"start": v(-18, 13.45) * mm, "end": v(-17.92, 13.65) * mm});
            skLineSegment(sketch, "E319", {"start": v(-17.92, 13.65) * mm, "end": v(-17.94, 14.11) * mm});
            skLineSegment(sketch, "E320", {"start": v(-17.94, 14.11) * mm, "end": v(-17.77, 14.54) * mm});
            skLineSegment(sketch, "E321", {"start": v(-17.77, 14.54) * mm, "end": v(-17.58, 15.1) * mm});
            skLineSegment(sketch, "E322", {"start": v(-17.58, 15.1) * mm, "end": v(-17.3, 15.32) * mm});
            skLineSegment(sketch, "E323", {"start": v(-17.3, 15.32) * mm, "end": v(-17.23, 15.72) * mm});
            skLineSegment(sketch, "E324", {"start": v(-17.23, 15.72) * mm, "end": v(-17.05, 16.27) * mm});
            skLineSegment(sketch, "E325", {"start": v(-17.05, 16.27) * mm, "end": v(-16.81, 16.54) * mm});
            skLineSegment(sketch, "E326", {"start": v(-16.81, 16.54) * mm, "end": v(-16.71, 16.99) * mm});
            skLineSegment(sketch, "E327", {"start": v(-16.71, 16.99) * mm, "end": v(-16.92, 17.33) * mm});
            skLineSegment(sketch, "E328", {"start": v(-16.92, 17.33) * mm, "end": v(-17, 17.37) * mm});
            skLineSegment(sketch, "E329", {"start": v(-17, 17.37) * mm, "end": v(-16.79, 17.92) * mm});
            skLineSegment(sketch, "E330", {"start": v(-16.79, 17.92) * mm, "end": v(-16.98, 18.4) * mm});
            skLineSegment(sketch, "E331", {"start": v(-16.98, 18.4) * mm, "end": v(-17.18, 18.56) * mm});
            skLineSegment(sketch, "E332", {"start": v(-17.18, 18.56) * mm, "end": v(-17.47, 18.51) * mm});
            skLineSegment(sketch, "E333", {"start": v(-17.47, 18.51) * mm, "end": v(-17.6, 18.76) * mm});
            skLineSegment(sketch, "E334", {"start": v(-17.6, 18.76) * mm, "end": v(-18.65, 19.83) * mm});
            skLineSegment(sketch, "E335", {"start": v(-18.65, 19.83) * mm, "end": v(-19.28, 20.18) * mm});
            skLineSegment(sketch, "E336", {"start": v(-19.28, 20.18) * mm, "end": v(-19.7, 20.25) * mm});
            skLineSegment(sketch, "E337", {"start": v(-19.7, 20.25) * mm, "end": v(-20.2, 20.09) * mm});
            skLineSegment(sketch, "E338", {"start": v(-20.2, 20.09) * mm, "end": v(-20.5, 19.9) * mm});
            skLineSegment(sketch, "E339", {"start": v(-20.5, 19.9) * mm, "end": v(-21.26, 19.27) * mm});
            skLineSegment(sketch, "E340", {"start": v(-21.26, 19.27) * mm, "end": v(-21.46, 18.83) * mm});
            skLineSegment(sketch, "E341", {"start": v(-21.46, 18.83) * mm, "end": v(-21.7, 18.41) * mm});
            skLineSegment(sketch, "E342", {"start": v(-21.7, 18.41) * mm, "end": v(-21.93, 18.02) * mm});
            skLineSegment(sketch, "E343", {"start": v(-21.93, 18.02) * mm, "end": v(-22.27, 17.35) * mm});
            skLineSegment(sketch, "E344", {"start": v(-22.27, 17.35) * mm, "end": v(-22.5, 16.58) * mm});
            skLineSegment(sketch, "E345", {"start": v(-22.5, 16.58) * mm, "end": v(-22.84, 15.63) * mm});
            skLineSegment(sketch, "E346", {"start": v(-22.84, 15.63) * mm, "end": v(-23.22, 14.64) * mm});
            skLineSegment(sketch, "E347", {"start": v(-23.22, 14.64) * mm, "end": v(-23.22, 14.33) * mm});
            skLineSegment(sketch, "E348", {"start": v(-23.22, 14.33) * mm, "end": v(-23.6, 12.81) * mm});
            skLineSegment(sketch, "E349", {"start": v(-23.6, 12.81) * mm, "end": v(-23.91, 11.62) * mm});
            skLineSegment(sketch, "E350", {"start": v(-23.91, 11.62) * mm, "end": v(-24.38, 10.24) * mm});
            skLineSegment(sketch, "E351", {"start": v(-24.38, 10.24) * mm, "end": v(-24.5, 9.57) * mm});
            skLineSegment(sketch, "E352", {"start": v(-24.5, 9.57) * mm, "end": v(-24.64, 8.65) * mm});
            skLineSegment(sketch, "E353", {"start": v(-24.64, 8.65) * mm, "end": v(-24.77, 8.13) * mm});
            skLineSegment(sketch, "E354", {"start": v(-24.77, 8.13) * mm, "end": v(-24.9, 7.38) * mm});
            skLineSegment(sketch, "E355", {"start": v(-24.9, 7.38) * mm, "end": v(-25, 6.76) * mm});
            skLineSegment(sketch, "E356", {"start": v(-25, 6.76) * mm, "end": v(-25.3, 5.08) * mm});
            skLineSegment(sketch, "E357", {"start": v(-25.3, 5.08) * mm, "end": v(-25.3, 3.81) * mm});
            skLineSegment(sketch, "E358", {"start": v(-25.3, 3.81) * mm, "end": v(-25.41, 2.51) * mm});
            skLineSegment(sketch, "E359", {"start": v(-25.41, 2.51) * mm, "end": v(-25.49, 0.85) * mm});
            skLineSegment(sketch, "E360", {"start": v(-25.49, 0.85) * mm, "end": v(-25.49, 0.18) * mm});
            skLineSegment(sketch, "E361", {"start": v(-25.49, 0.18) * mm, "end": v(-25.41, -0.81) * mm});
            skLineSegment(sketch, "E362", {"start": v(-25.41, -0.81) * mm, "end": v(-25.38, -1.61) * mm});
            skLineSegment(sketch, "E363", {"start": v(-25.38, -1.61) * mm, "end": v(-25.24, -2.15) * mm});
            skLineSegment(sketch, "E364", {"start": v(-25.24, -2.15) * mm, "end": v(-24.97, -2.52) * mm});
            skLineSegment(sketch, "E365", {"start": v(-24.97, -2.52) * mm, "end": v(-24.42, -2.85) * mm});
            skLineSegment(sketch, "E366", {"start": v(-24.42, -2.85) * mm, "end": v(-24, -2.75) * mm});
            skLineSegment(sketch, "E367", {"start": v(-24, -2.75) * mm, "end": v(-23.64, -2.5) * mm});
            skLineSegment(sketch, "E368", {"start": v(-23.64, -2.5) * mm, "end": v(-23.3, -2.24) * mm});
            skLineSegment(sketch, "E369", {"start": v(-23.3, -2.24) * mm, "end": v(-22.68, -1.78) * mm});
            skLineSegment(sketch, "E370", {"start": v(-22.68, -1.78) * mm, "end": v(-21.17, -0.13) * mm});
            skLineSegment(sketch, "E371", {"start": v(-21.17, -0.13) * mm, "end": v(-20.68, 0.44) * mm});
            skLineSegment(sketch, "E372", {"start": v(-20.68, 0.44) * mm, "end": v(-20.14, 1.33) * mm});
            skLineSegment(sketch, "E373", {"start": v(-20.14, 1.33) * mm, "end": v(-20.01, 1.55) * mm});
            skLineSegment(sketch, "E374", {"start": v(-20.01, 1.55) * mm, "end": v(-20.19, 1.8) * mm});
            skLineSegment(sketch, "E375", {"start": v(-20.19, 1.8) * mm, "end": v(-20.33, 1.9) * mm});
            skLineSegment(sketch, "E376", {"start": v(-20.33, 1.9) * mm, "end": v(-20.54, 1.91) * mm});
            skLineSegment(sketch, "E377", {"start": v(-20.54, 1.91) * mm, "end": v(-20.68, 1.76) * mm});
            skLineSegment(sketch, "E378", {"start": v(-20.68, 1.76) * mm, "end": v(-20.68, 1.53) * mm});
            skLineSegment(sketch, "E379", {"start": v(-20.68, 1.53) * mm, "end": v(-20.75, 1.43) * mm});
            skLineSegment(sketch, "E380", {"start": v(-20.75, 1.43) * mm, "end": v(-21, 1.24) * mm});
            skLineSegment(sketch, "E381", {"start": v(-21, 1.24) * mm, "end": v(-21.08, 0.93) * mm});
            skLineSegment(sketch, "E382", {"start": v(-21.08, 0.93) * mm, "end": v(-21.37, 0.7) * mm});
            skLineSegment(sketch, "E383", {"start": v(-21.37, 0.7) * mm, "end": v(-21.86, 0.18) * mm});
            skLineSegment(sketch, "E384", {"start": v(-21.86, 0.18) * mm, "end": v(-22.38, -0.51) * mm});
            skLineSegment(sketch, "E385", {"start": v(-22.38, -0.51) * mm, "end": v(-22.96, -1.12) * mm});
            skLineSegment(sketch, "E386", {"start": v(-22.96, -1.12) * mm, "end": v(-23.5, -1.59) * mm});
            skLineSegment(sketch, "E387", {"start": v(-23.5, -1.59) * mm, "end": v(-23.75, -1.78) * mm});
            skLineSegment(sketch, "E388", {"start": v(-23.75, -1.78) * mm, "end": v(-24.54, -1.72) * mm});
            skLineSegment(sketch, "E389", {"start": v(-24.54, -1.72) * mm, "end": v(-24.76, -1.46) * mm});
            skLineSegment(sketch, "E390", {"start": v(-24.76, -1.46) * mm, "end": v(-24.98, -0.97) * mm});
            skLineSegment(sketch, "E391", {"start": v(-24.98, -0.97) * mm, "end": v(-24.98, -0.49) * mm});
            skLineSegment(sketch, "E392", {"start": v(-24.98, -0.49) * mm, "end": v(-24.98, 0.32) * mm});
            skLineSegment(sketch, "E393", {"start": v(-24.98, 0.32) * mm, "end": v(-24.9, 2.51) * mm});
            skLineSegment(sketch, "E394", {"start": v(-24.9, 2.51) * mm, "end": v(-24.85, 3.44) * mm});
            skLineSegment(sketch, "E395", {"start": v(-24.85, 3.44) * mm, "end": v(-24.6, 5.5) * mm});
            skLineSegment(sketch, "E396", {"start": v(-24.6, 5.5) * mm, "end": v(-24.43, 5.93) * mm});
            skLineSegment(sketch, "E397", {"start": v(-24.43, 5.93) * mm, "end": v(-24.3, 6.73) * mm});
            skLineSegment(sketch, "E398", {"start": v(-24.3, 6.73) * mm, "end": v(-24.3, 7.22) * mm});
            skLineSegment(sketch, "E399", {"start": v(-24.3, 7.22) * mm, "end": v(-24.15, 8.05) * mm});
            skLineSegment(sketch, "E400", {"start": v(-24.15, 8.05) * mm, "end": v(-23.8, 9.1) * mm});
            skLineSegment(sketch, "E401", {"start": v(-23.8, 9.1) * mm, "end": v(-23.67, 9.36) * mm});
            skLineSegment(sketch, "E402", {"start": v(-23.67, 9.36) * mm, "end": v(-23.62, 9.6) * mm});
            skLineSegment(sketch, "E403", {"start": v(-23.62, 9.6) * mm, "end": v(-23.6, 9.84) * mm});
            skLineSegment(sketch, "E404", {"start": v(-23.6, 9.84) * mm, "end": v(-23.37, 10.2) * mm});
            skLineSegment(sketch, "E405", {"start": v(-23.37, 10.2) * mm, "end": v(-23.12, 10.9) * mm});
            skLineSegment(sketch, "E406", {"start": v(-23.12, 10.9) * mm, "end": v(-22.9, 11.39) * mm});
            skLineSegment(sketch, "E407", {"start": v(-22.9, 11.39) * mm, "end": v(-22.62, 12.31) * mm});
            skLineSegment(sketch, "E408", {"start": v(-22.62, 12.31) * mm, "end": v(-22.33, 13.13) * mm});
            skLineSegment(sketch, "E409", {"start": v(-22.33, 13.13) * mm, "end": v(-21.93, 14.14) * mm});
            skLineSegment(sketch, "E410", {"start": v(-21.93, 14.14) * mm, "end": v(-21.77, 14.87) * mm});
            skLineSegment(sketch, "E411", {"start": v(-21.77, 14.87) * mm, "end": v(-21.4, 15.47) * mm});
            skLineSegment(sketch, "E412", {"start": v(-21.4, 15.47) * mm, "end": v(-21, 15.51) * mm});
            skLineSegment(sketch, "E413", {"start": v(-21, 15.51) * mm, "end": v(-20.7, 16.16) * mm});
            skLineSegment(sketch, "E414", {"start": v(-20.7, 16.16) * mm, "end": v(-20.95, 16.68) * mm});
            skLineSegment(sketch, "E415", {"start": v(-20.95, 16.68) * mm, "end": v(-21.1, 16.65) * mm});
            skLineSegment(sketch, "E416", {"start": v(-21.1, 16.65) * mm, "end": v(-20.69, 17.34) * mm});
            skLineSegment(sketch, "E417", {"start": v(-20.69, 17.34) * mm, "end": v(-20.46, 17.76) * mm});
            skLineSegment(sketch, "E418", {"start": v(-20.46, 17.76) * mm, "end": v(-20.2, 17.92) * mm});
            skLineSegment(sketch, "E419", {"start": v(-20.72, 5.51) * mm, "end": v(-20.16, 6.07) * mm});
            skLineSegment(sketch, "E420", {"start": v(-20.16, 6.07) * mm, "end": v(-19.7, 6.63) * mm});
            skLineSegment(sketch, "E421", {"start": v(-19.7, 6.63) * mm, "end": v(-19.12, 7.6) * mm});
            skLineSegment(sketch, "E422", {"start": v(-19.12, 7.6) * mm, "end": v(-18.72, 8.44) * mm});
            skLineSegment(sketch, "E423", {"start": v(-18.72, 8.44) * mm, "end": v(-18.53, 8.77) * mm});
            skLineSegment(sketch, "E424", {"start": v(-18.53, 8.77) * mm, "end": v(-18.66, 9.45) * mm});
            skLineSegment(sketch, "E425", {"start": v(-18.66, 9.45) * mm, "end": v(-18.81, 9.6) * mm});
            skLineSegment(sketch, "E426", {"start": v(-18.81, 9.6) * mm, "end": v(-18.76, 9.93) * mm});
            skLineSegment(sketch, "E427", {"start": v(-18.76, 9.93) * mm, "end": v(-18.06, 10.27) * mm});
            skLineSegment(sketch, "E428", {"start": v(-18.06, 10.27) * mm, "end": v(-17.58, 10.6) * mm});
            skLineSegment(sketch, "E429", {"start": v(-17.58, 10.6) * mm, "end": v(-17.08, 10.75) * mm});
            skLineSegment(sketch, "E430", {"start": v(-17.08, 10.75) * mm, "end": v(-16.83, 10.64) * mm});
            skLineSegment(sketch, "E431", {"start": v(-16.83, 10.64) * mm, "end": v(-16.86, 9.91) * mm});
            skLineSegment(sketch, "E432", {"start": v(-16.86, 9.91) * mm, "end": v(-16.54, 9.71) * mm});
            skLineSegment(sketch, "E433", {"start": v(-16.54, 9.71) * mm, "end": v(-16.16, 9.54) * mm});
            skLineSegment(sketch, "E434", {"start": v(-16.16, 9.54) * mm, "end": v(-15.83, 9.31) * mm});
            skLineSegment(sketch, "E435", {"start": v(-15.83, 9.31) * mm, "end": v(-15.33, 8.46) * mm});
            skLineSegment(sketch, "E436", {"start": v(-15.33, 8.46) * mm, "end": v(-15.55, 7.79) * mm});
            skLineSegment(sketch, "E437", {"start": v(-15.55, 7.79) * mm, "end": v(-15.82, 6.91) * mm});
            skLineSegment(sketch, "E438", {"start": v(-15.82, 6.91) * mm, "end": v(-16.22, 6.36) * mm});
            skLineSegment(sketch, "E439", {"start": v(-16.22, 6.36) * mm, "end": v(-16.44, 5.84) * mm});
            skLineSegment(sketch, "E440", {"start": v(-16.44, 5.84) * mm, "end": v(-16.77, 5.19) * mm});
            skLineSegment(sketch, "E441", {"start": v(-16.77, 5.19) * mm, "end": v(-16.78, 4.65) * mm});
            skLineSegment(sketch, "E442", {"start": v(-16.78, 4.65) * mm, "end": v(-16.64, 4.28) * mm});
            skLineSegment(sketch, "E443", {"start": v(-16.64, 4.28) * mm, "end": v(-16.45, 3.98) * mm});
            skLineSegment(sketch, "E444", {"start": v(-16.45, 3.98) * mm, "end": v(-16.4, 3.88) * mm});
            skLineSegment(sketch, "E445", {"start": v(-16.4, 3.88) * mm, "end": v(-17.14, 3.26) * mm});
            skLineSegment(sketch, "E446", {"start": v(-17.14, 3.26) * mm, "end": v(-17.45, 3.2) * mm});
            skLineSegment(sketch, "E447", {"start": v(-17.45, 3.2) * mm, "end": v(-17.76, 3.22) * mm});
            skLineSegment(sketch, "E448", {"start": v(-17.76, 3.22) * mm, "end": v(-17.98, 3.3) * mm});
            skLineSegment(sketch, "E449", {"start": v(-17.98, 3.3) * mm, "end": v(-18.16, 3.45) * mm});
            skLineSegment(sketch, "E450", {"start": v(-18.16, 3.45) * mm, "end": v(-18.18, 3.64) * mm});
            skLineSegment(sketch, "E451", {"start": v(-18.18, 3.64) * mm, "end": v(-18.22, 3.73) * mm});
            skLineSegment(sketch, "E452", {"start": v(-18.22, 3.73) * mm, "end": v(-18.2, 4.03) * mm});
            skLineSegment(sketch, "E453", {"start": v(-18.2, 4.03) * mm, "end": v(-18.14, 4.26) * mm});
            skLineSegment(sketch, "E454", {"start": v(-18.14, 4.26) * mm, "end": v(-18.11, 4.46) * mm});
            skLineSegment(sketch, "E455", {"start": v(-18.11, 4.46) * mm, "end": v(-18.08, 4.62) * mm});
            skLineSegment(sketch, "E456", {"start": v(-18.08, 4.62) * mm, "end": v(-18, 4.85) * mm});
            skLineSegment(sketch, "E457", {"start": v(-18, 4.85) * mm, "end": v(-17.95, 4.96) * mm});
            skLineSegment(sketch, "E458", {"start": v(-17.95, 4.96) * mm, "end": v(-17.87, 5.43) * mm});
            skLineSegment(sketch, "E459", {"start": v(-17.87, 5.43) * mm, "end": v(-17.75, 5.63) * mm});
            skLineSegment(sketch, "E460", {"start": v(-17.75, 5.63) * mm, "end": v(-17.56, 5.88) * mm});
            skLineSegment(sketch, "E461", {"start": v(-17.56, 5.88) * mm, "end": v(-17.5, 6.12) * mm});
            skLineSegment(sketch, "E462", {"start": v(-17.5, 6.12) * mm, "end": v(-17.53, 6.4) * mm});
            skLineSegment(sketch, "E463", {"start": v(-17.53, 6.4) * mm, "end": v(-17.34, 6.58) * mm});
            skLineSegment(sketch, "E464", {"start": v(-17.34, 6.58) * mm, "end": v(-17.26, 7.02) * mm});
            skLineSegment(sketch, "E465", {"start": v(-17.26, 7.02) * mm, "end": v(-17.14, 7.4) * mm});
            skLineSegment(sketch, "E466", {"start": v(-17.14, 7.4) * mm, "end": v(-17.11, 7.61) * mm});
            skLineSegment(sketch, "E467", {"start": v(-17.11, 7.61) * mm, "end": v(-17.11, 7.84) * mm});
            skLineSegment(sketch, "E468", {"start": v(-17.11, 7.84) * mm, "end": v(-17.11, 8) * mm});
            skLineSegment(sketch, "E469", {"start": v(-17.11, 8) * mm, "end": v(-17.4, 8.42) * mm});
            skLineSegment(sketch, "E470", {"start": v(-17.4, 8.42) * mm, "end": v(-17.58, 8.5) * mm});
            skLineSegment(sketch, "E471", {"start": v(-17.58, 8.5) * mm, "end": v(-18.08, 7.88) * mm});
            skLineSegment(sketch, "E472", {"start": v(-18.08, 7.88) * mm, "end": v(-18.37, 7.5) * mm});
            skLineSegment(sketch, "E473", {"start": v(-18.37, 7.5) * mm, "end": v(-18.37, 7.44) * mm});
            skLineSegment(sketch, "E474", {"start": v(-18.37, 7.44) * mm, "end": v(-18.53, 7.24) * mm});
            skLineSegment(sketch, "E475", {"start": v(-18.53, 7.24) * mm, "end": v(-18.67, 7.03) * mm});
            skLineSegment(sketch, "E476", {"start": v(-18.67, 7.03) * mm, "end": v(-18.98, 6.65) * mm});
            skLineSegment(sketch, "E477", {"start": v(-18.98, 6.65) * mm, "end": v(-19.28, 6.3) * mm});
            skLineSegment(sketch, "E478", {"start": v(-19.28, 6.3) * mm, "end": v(-19.45, 6.08) * mm});
            skLineSegment(sketch, "E479", {"start": v(-19.45, 6.08) * mm, "end": v(-19.61, 5.91) * mm});
            skLineSegment(sketch, "E480", {"start": v(-19.61, 5.91) * mm, "end": v(-20.1, 5.52) * mm});
            skLineSegment(sketch, "E481", {"start": v(-20.1, 5.52) * mm, "end": v(-20.27, 5.33) * mm});
            skLineSegment(sketch, "E482", {"start": v(-20.27, 5.33) * mm, "end": v(-20.4, 5.27) * mm});
            skLineSegment(sketch, "E483", {"start": v(-20.4, 5.27) * mm, "end": v(-20.66, 5.06) * mm});
            skLineSegment(sketch, "E484", {"start": v(-20.66, 5.06) * mm, "end": v(-20.75, 5.27) * mm});
            skLineSegment(sketch, "E485", {"start": v(-20.75, 5.27) * mm, "end": v(-20.72, 5.51) * mm});
            skLineSegment(sketch, "E486", {"start": v(-14.61, 6.58) * mm, "end": v(-14.91, 4.96) * mm});
            skLineSegment(sketch, "E487", {"start": v(-14.91, 4.96) * mm, "end": v(-14.94, 4.26) * mm});
            skLineSegment(sketch, "E488", {"start": v(-14.94, 4.26) * mm, "end": v(-15.1, 3.78) * mm});
            skLineSegment(sketch, "E489", {"start": v(-15.1, 3.78) * mm, "end": v(-14.41, 2.93) * mm});
            skLineSegment(sketch, "E490", {"start": v(-14.41, 2.93) * mm, "end": v(-13.76, 2.46) * mm});
            skLineSegment(sketch, "E491", {"start": v(-13.76, 2.46) * mm, "end": v(-13.06, 2.51) * mm});
            skLineSegment(sketch, "E492", {"start": v(-13.06, 2.51) * mm, "end": v(-12.58, 2.75) * mm});
            skLineSegment(sketch, "E493", {"start": v(-12.58, 2.75) * mm, "end": v(-11.84, 3.27) * mm});
            skLineSegment(sketch, "E494", {"start": v(-11.84, 3.27) * mm, "end": v(-11.25, 4.03) * mm});
            skLineSegment(sketch, "E495", {"start": v(-11.25, 4.03) * mm, "end": v(-10.66, 5.26) * mm});
            skLineSegment(sketch, "E496", {"start": v(-10.66, 5.26) * mm, "end": v(-10.26, 6.06) * mm});
            skLineSegment(sketch, "E497", {"start": v(-10.26, 6.06) * mm, "end": v(-10.07, 7.12) * mm});
            skLineSegment(sketch, "E498", {"start": v(-10.07, 7.12) * mm, "end": v(-9.96, 7.68) * mm});
            skLineSegment(sketch, "E499", {"start": v(-9.96, 7.68) * mm, "end": v(-9.96, 8.02) * mm});
            skLineSegment(sketch, "E500", {"start": v(-9.96, 8.02) * mm, "end": v(-10, 8.22) * mm});
            skLineSegment(sketch, "E501", {"start": v(-10, 8.22) * mm, "end": v(-10.34, 8.76) * mm});
            skLineSegment(sketch, "E502", {"start": v(-10.34, 8.76) * mm, "end": v(-10.63, 9.01) * mm});
            skLineSegment(sketch, "E503", {"start": v(-10.63, 9.01) * mm, "end": v(-10.95, 9.14) * mm});
            skLineSegment(sketch, "E504", {"start": v(-10.95, 9.14) * mm, "end": v(-11.45, 8.95) * mm});
            skLineSegment(sketch, "E505", {"start": v(-11.45, 8.95) * mm, "end": v(-11.79, 8.8) * mm});
            skLineSegment(sketch, "E506", {"start": v(-11.79, 8.8) * mm, "end": v(-12.2, 8.63) * mm});
            skLineSegment(sketch, "E507", {"start": v(-12.2, 8.63) * mm, "end": v(-12.54, 8.41) * mm});
            skLineSegment(sketch, "E508", {"start": v(-12.54, 8.41) * mm, "end": v(-12.93, 8.22) * mm});
            skLineSegment(sketch, "E509", {"start": v(-12.93, 8.22) * mm, "end": v(-13.27, 7.98) * mm});
            skLineSegment(sketch, "E510", {"start": v(-13.27, 7.98) * mm, "end": v(-13.57, 7.62) * mm});
            skLineSegment(sketch, "E511", {"start": v(-13.57, 7.62) * mm, "end": v(-13.68, 7.42) * mm});
            skLineSegment(sketch, "E512", {"start": v(-13.68, 7.42) * mm, "end": v(-14.04, 6.98) * mm});
            skLineSegment(sketch, "E513", {"start": v(-14.04, 6.98) * mm, "end": v(-14.39, 6.7) * mm});
            skLineSegment(sketch, "E514", {"start": v(-14.39, 6.7) * mm, "end": v(-14.62, 6.6) * mm});
            skLineSegment(sketch, "E515", {"start": v(-14.62, 6.6) * mm, "end": v(-14.61, 6.58) * mm});
            skLineSegment(sketch, "E516", {"start": v(-13.09, 6.47) * mm, "end": v(-13.04, 6.1) * mm});
            skLineSegment(sketch, "E517", {"start": v(-13.04, 6.1) * mm, "end": v(-13.07, 5.44) * mm});
            skLineSegment(sketch, "E518", {"start": v(-13.07, 5.44) * mm, "end": v(-13.2, 5.32) * mm});
            skLineSegment(sketch, "E519", {"start": v(-13.2, 5.32) * mm, "end": v(-13.19, 5.22) * mm});
            skLineSegment(sketch, "E520", {"start": v(-13.19, 5.22) * mm, "end": v(-13.1, 5.22) * mm});
            skLineSegment(sketch, "E521", {"start": v(-13.1, 5.22) * mm, "end": v(-13.25, 4.96) * mm});
            skLineSegment(sketch, "E522", {"start": v(-13.25, 4.96) * mm, "end": v(-13.28, 4.63) * mm});
            skLineSegment(sketch, "E523", {"start": v(-13.28, 4.63) * mm, "end": v(-13.31, 4.4) * mm});
            skLineSegment(sketch, "E524", {"start": v(-13.31, 4.4) * mm, "end": v(-13.2, 4.22) * mm});
            skLineSegment(sketch, "E525", {"start": v(-13.2, 4.22) * mm, "end": v(-12.95, 3.99) * mm});
            skLineSegment(sketch, "E526", {"start": v(-12.95, 3.99) * mm, "end": v(-12.7, 3.92) * mm});
            skLineSegment(sketch, "E527", {"start": v(-12.7, 3.92) * mm, "end": v(-12.57, 3.98) * mm});
            skLineSegment(sketch, "E528", {"start": v(-12.57, 3.98) * mm, "end": v(-12.4, 4.22) * mm});
            skLineSegment(sketch, "E529", {"start": v(-12.4, 4.22) * mm, "end": v(-12.3, 4.4) * mm});
            skLineSegment(sketch, "E530", {"start": v(-12.3, 4.4) * mm, "end": v(-12.26, 4.47) * mm});
            skLineSegment(sketch, "E531", {"start": v(-12.26, 4.47) * mm, "end": v(-12.1, 4.67) * mm});
            skLineSegment(sketch, "E532", {"start": v(-12.1, 4.67) * mm, "end": v(-11.65, 5.14) * mm});
            skLineSegment(sketch, "E533", {"start": v(-11.65, 5.14) * mm, "end": v(-11.52, 5.41) * mm});
            skLineSegment(sketch, "E534", {"start": v(-11.52, 5.41) * mm, "end": v(-11.5, 5.47) * mm});
            skLineSegment(sketch, "E535", {"start": v(-11.5, 5.47) * mm, "end": v(-11.4, 5.68) * mm});
            skLineSegment(sketch, "E536", {"start": v(-11.4, 5.68) * mm, "end": v(-11.38, 5.84) * mm});
            skLineSegment(sketch, "E537", {"start": v(-11.38, 5.84) * mm, "end": v(-11.36, 5.94) * mm});
            skLineSegment(sketch, "E538", {"start": v(-11.36, 5.94) * mm, "end": v(-11.35, 6.3) * mm});
            skLineSegment(sketch, "E539", {"start": v(-11.35, 6.3) * mm, "end": v(-11.36, 6.49) * mm});
            skLineSegment(sketch, "E540", {"start": v(-11.36, 6.49) * mm, "end": v(-11.52, 6.57) * mm});
            skLineSegment(sketch, "E541", {"start": v(-11.52, 6.57) * mm, "end": v(-11.75, 6.84) * mm});
            skLineSegment(sketch, "E542", {"start": v(-11.75, 6.84) * mm, "end": v(-11.96, 6.95) * mm});
            skLineSegment(sketch, "E543", {"start": v(-11.96, 6.95) * mm, "end": v(-12.2, 7) * mm});
            skLineSegment(sketch, "E544", {"start": v(-12.2, 7) * mm, "end": v(-12.64, 7.02) * mm});
            skLineSegment(sketch, "E545", {"start": v(-12.64, 7.02) * mm, "end": v(-12.93, 6.8) * mm});
            skLineSegment(sketch, "E546", {"start": v(-12.93, 6.8) * mm, "end": v(-12.93, 6.7) * mm});
            skLineSegment(sketch, "E547", {"start": v(-12.93, 6.7) * mm, "end": v(-12.91, 6.57) * mm});
            skLineSegment(sketch, "E548", {"start": v(-12.91, 6.57) * mm, "end": v(-13.07, 6.43) * mm});
            skLineSegment(sketch, "E549", {"start": v(-13.07, 6.43) * mm, "end": v(-13.08, 6.48) * mm});
            skLineSegment(sketch, "E550", {"start": v(-13.08, 6.48) * mm, "end": v(-13.09, 6.47) * mm});
            skLineSegment(sketch, "E551", {"start": v(-10.5, 3.7) * mm, "end": v(-9.57, 4.6) * mm});
            skLineSegment(sketch, "E552", {"start": v(-9.57, 4.6) * mm, "end": v(-8.7, 5.6) * mm});
            skLineSegment(sketch, "E553", {"start": v(-8.7, 5.6) * mm, "end": v(-8.36, 6.02) * mm});
            skLineSegment(sketch, "E554", {"start": v(-8.36, 6.02) * mm, "end": v(-8.02, 6.3) * mm});
            skLineSegment(sketch, "E555", {"start": v(-8.02, 6.3) * mm, "end": v(-7.8, 6.83) * mm});
            skLineSegment(sketch, "E556", {"start": v(-7.8, 6.83) * mm, "end": v(-7.17, 7.8) * mm});
            skLineSegment(sketch, "E557", {"start": v(-7.17, 7.8) * mm, "end": v(-6.67, 8.17) * mm});
            skLineSegment(sketch, "E558", {"start": v(-6.67, 8.17) * mm, "end": v(-6.28, 8.38) * mm});
            skLineSegment(sketch, "E559", {"start": v(-6.28, 8.38) * mm, "end": v(-5.89, 8.56) * mm});
            skLineSegment(sketch, "E560", {"start": v(-5.89, 8.56) * mm, "end": v(-5.53, 8.63) * mm});
            skLineSegment(sketch, "E561", {"start": v(-5.53, 8.63) * mm, "end": v(-5.33, 8.54) * mm});
            skLineSegment(sketch, "E562", {"start": v(-5.33, 8.54) * mm, "end": v(-5.33, 8.38) * mm});
            skLineSegment(sketch, "E563", {"start": v(-5.33, 8.38) * mm, "end": v(-5.42, 8.03) * mm});
            skLineSegment(sketch, "E564", {"start": v(-5.42, 8.03) * mm, "end": v(-5.52, 7.82) * mm});
            skLineSegment(sketch, "E565", {"start": v(-5.52, 7.82) * mm, "end": v(-5.64, 7.5) * mm});
            skLineSegment(sketch, "E566", {"start": v(-5.64, 7.5) * mm, "end": v(-5.73, 7.15) * mm});
            skLineSegment(sketch, "E567", {"start": v(-5.73, 7.15) * mm, "end": v(-5.95, 6.57) * mm});
            skLineSegment(sketch, "E568", {"start": v(-5.95, 6.57) * mm, "end": v(-6.07, 6.12) * mm});
            skLineSegment(sketch, "E569", {"start": v(-6.07, 6.12) * mm, "end": v(-6.14, 4.36) * mm});
            skLineSegment(sketch, "E570", {"start": v(-6.14, 4.36) * mm, "end": v(-5.8, 4.15) * mm});
            skLineSegment(sketch, "E571", {"start": v(-5.8, 4.15) * mm, "end": v(-5.58, 4.12) * mm});
            skLineSegment(sketch, "E572", {"start": v(-5.58, 4.12) * mm, "end": v(-5.2, 4.36) * mm});
            skLineSegment(sketch, "E573", {"start": v(-5.2, 4.36) * mm, "end": v(-5, 4.44) * mm});
            skLineSegment(sketch, "E574", {"start": v(-5, 4.44) * mm, "end": v(-4.72, 4.72) * mm});
            skLineSegment(sketch, "E575", {"start": v(-4.72, 4.72) * mm, "end": v(-4.52, 4.77) * mm});
            skLineSegment(sketch, "E576", {"start": v(-4.52, 4.77) * mm, "end": v(-4.44, 4.48) * mm});
            skLineSegment(sketch, "E577", {"start": v(-4.44, 4.48) * mm, "end": v(-4.47, 4.2) * mm});
            skLineSegment(sketch, "E578", {"start": v(-4.47, 4.2) * mm, "end": v(-4.7, 4) * mm});
            skLineSegment(sketch, "E579", {"start": v(-4.7, 4) * mm, "end": v(-5.21, 3.6) * mm});
            skLineSegment(sketch, "E580", {"start": v(-5.21, 3.6) * mm, "end": v(-5.48, 3.42) * mm});
            skLineSegment(sketch, "E581", {"start": v(-5.48, 3.42) * mm, "end": v(-5.92, 3.28) * mm});
            skLineSegment(sketch, "E582", {"start": v(-5.92, 3.28) * mm, "end": v(-6.27, 3.13) * mm});
            skLineSegment(sketch, "E583", {"start": v(-6.27, 3.13) * mm, "end": v(-6.76, 3.08) * mm});
            skLineSegment(sketch, "E584", {"start": v(-6.76, 3.08) * mm, "end": v(-7.05, 3.1) * mm});
            skLineSegment(sketch, "E585", {"start": v(-7.05, 3.1) * mm, "end": v(-7.3, 3.13) * mm});
            skLineSegment(sketch, "E586", {"start": v(-7.3, 3.13) * mm, "end": v(-7.51, 3.16) * mm});
            skLineSegment(sketch, "E587", {"start": v(-7.51, 3.16) * mm, "end": v(-7.6, 3.2) * mm});
            skLineSegment(sketch, "E588", {"start": v(-7.6, 3.2) * mm, "end": v(-7.86, 3.45) * mm});
            skLineSegment(sketch, "E589", {"start": v(-7.86, 3.45) * mm, "end": v(-7.9, 3.68) * mm});
            skLineSegment(sketch, "E590", {"start": v(-7.9, 3.68) * mm, "end": v(-7.95, 4) * mm});
            skLineSegment(sketch, "E591", {"start": v(-7.95, 4) * mm, "end": v(-7.94, 4.18) * mm});
            skLineSegment(sketch, "E592", {"start": v(-7.94, 4.18) * mm, "end": v(-7.95, 4.43) * mm});
            skLineSegment(sketch, "E593", {"start": v(-7.95, 4.43) * mm, "end": v(-8.02, 4.57) * mm});
            skLineSegment(sketch, "E594", {"start": v(-8.02, 4.57) * mm, "end": v(-8.25, 4.69) * mm});
            skLineSegment(sketch, "E595", {"start": v(-8.25, 4.69) * mm, "end": v(-8.39, 4.66) * mm});
            skLineSegment(sketch, "E596", {"start": v(-8.39, 4.66) * mm, "end": v(-8.62, 4.55) * mm});
            skLineSegment(sketch, "E597", {"start": v(-8.62, 4.55) * mm, "end": v(-8.77, 4.47) * mm});
            skLineSegment(sketch, "E598", {"start": v(-8.77, 4.47) * mm, "end": v(-9.37, 4.13) * mm});
            skLineSegment(sketch, "E599", {"start": v(-9.37, 4.13) * mm, "end": v(-9.7, 3.95) * mm});
            skLineSegment(sketch, "E600", {"start": v(-9.7, 3.95) * mm, "end": v(-9.87, 3.85) * mm});
            skLineSegment(sketch, "E601", {"start": v(-9.87, 3.85) * mm, "end": v(-10.13, 3.69) * mm});
            skLineSegment(sketch, "E602", {"start": v(-10.13, 3.69) * mm, "end": v(-10.28, 3.58) * mm});
            skLineSegment(sketch, "E603", {"start": v(-10.28, 3.58) * mm, "end": v(-10.37, 3.53) * mm});
            skLineSegment(sketch, "E604", {"start": v(-10.37, 3.53) * mm, "end": v(-10.46, 3.52) * mm});
            skLineSegment(sketch, "E605", {"start": v(-10.46, 3.52) * mm, "end": v(-10.46, 3.58) * mm});
            skLineSegment(sketch, "E606", {"start": v(-10.46, 3.58) * mm, "end": v(-10.5, 3.7) * mm});
            skLineSegment(sketch, "E607", {"start": v(-7.75, -0.18) * mm, "end": v(-6.5, 1.07) * mm});
            skLineSegment(sketch, "E608", {"start": v(-6.5, 1.07) * mm, "end": v(-5.47, 1.8) * mm});
            skLineSegment(sketch, "E609", {"start": v(-5.47, 1.8) * mm, "end": v(-4.26, 3) * mm});
            skLineSegment(sketch, "E610", {"start": v(-4.26, 3) * mm, "end": v(-3.33, 4.27) * mm});
            skLineSegment(sketch, "E611", {"start": v(-3.33, 4.27) * mm, "end": v(-1.95, 6.5) * mm});
            skLineSegment(sketch, "E612", {"start": v(-1.95, 6.5) * mm, "end": v(-1.86, 6.97) * mm});
            skLineSegment(sketch, "E613", {"start": v(-1.86, 6.97) * mm, "end": v(-2.13, 7.46) * mm});
            skLineSegment(sketch, "E614", {"start": v(-2.13, 7.46) * mm, "end": v(-2.21, 8.16) * mm});
            skLineSegment(sketch, "E615", {"start": v(-2.21, 8.16) * mm, "end": v(-2.15, 8.54) * mm});
            skLineSegment(sketch, "E616", {"start": v(-2.15, 8.54) * mm, "end": v(-2.3, 9) * mm});
            skLineSegment(sketch, "E617", {"start": v(-2.3, 9) * mm, "end": v(-2.3, 9.38) * mm});
            skLineSegment(sketch, "E618", {"start": v(-2.3, 9.38) * mm, "end": v(-2.3, 10.58) * mm});
            skLineSegment(sketch, "E619", {"start": v(-2.3, 10.58) * mm, "end": v(-2.3, 11.22) * mm});
            skLineSegment(sketch, "E620", {"start": v(-2.3, 11.22) * mm, "end": v(-2.05, 12.02) * mm});
            skLineSegment(sketch, "E621", {"start": v(-2.05, 12.02) * mm, "end": v(-1.68, 12.68) * mm});
            skLineSegment(sketch, "E622", {"start": v(-1.68, 12.68) * mm, "end": v(-1.3, 12.91) * mm});
            skLineSegment(sketch, "E623", {"start": v(-1.3, 12.91) * mm, "end": v(-1.16, 12.65) * mm});
            skLineSegment(sketch, "E624", {"start": v(-1.16, 12.65) * mm, "end": v(-1.2, 11.95) * mm});
            skLineSegment(sketch, "E625", {"start": v(-1.2, 11.95) * mm, "end": v(-1.27, 11.63) * mm});
            skLineSegment(sketch, "E626", {"start": v(-1.27, 11.63) * mm, "end": v(-1.23, 10.97) * mm});
            skLineSegment(sketch, "E627", {"start": v(-1.23, 10.97) * mm, "end": v(-1.13, 10.62) * mm});
            skLineSegment(sketch, "E628", {"start": v(-1.13, 10.62) * mm, "end": v(-0.73, 10.05) * mm});
            skLineSegment(sketch, "E629", {"start": v(-0.73, 10.05) * mm, "end": v(-0.9, 9.83) * mm});
            skLineSegment(sketch, "E630", {"start": v(-0.9, 9.83) * mm, "end": v(-1.04, 9.25) * mm});
            skLineSegment(sketch, "E631", {"start": v(-1.04, 9.25) * mm, "end": v(-0.89, 8.18) * mm});
            skLineSegment(sketch, "E632", {"start": v(-0.89, 8.18) * mm, "end": v(-0.85, 8.11) * mm});
            skLineSegment(sketch, "E633", {"start": v(-0.85, 8.11) * mm, "end": v(-0.81, 8.03) * mm});
            skLineSegment(sketch, "E634", {"start": v(-0.81, 8.03) * mm, "end": v(-0.65, 8.08) * mm});
            skLineSegment(sketch, "E635", {"start": v(-0.65, 8.08) * mm, "end": v(0.67, 9.84) * mm});
            skLineSegment(sketch, "E636", {"start": v(0.67, 9.84) * mm, "end": v(1.85, 11.8) * mm});
            skLineSegment(sketch, "E637", {"start": v(1.85, 11.8) * mm, "end": v(2.57, 12.7) * mm});
            skLineSegment(sketch, "E638", {"start": v(2.57, 12.7) * mm, "end": v(3.1, 12.8) * mm});
            skLineSegment(sketch, "E639", {"start": v(3.1, 12.8) * mm, "end": v(3.38, 12.5) * mm});
            skLineSegment(sketch, "E640", {"start": v(3.38, 12.5) * mm, "end": v(3.5, 11.82) * mm});
            skLineSegment(sketch, "E641", {"start": v(3.5, 11.82) * mm, "end": v(3.16, 10.96) * mm});
            skLineSegment(sketch, "E642", {"start": v(3.16, 10.96) * mm, "end": v(2.83, 10.49) * mm});
            skLineSegment(sketch, "E643", {"start": v(2.83, 10.49) * mm, "end": v(2.47, 9.89) * mm});
            skLineSegment(sketch, "E644", {"start": v(2.47, 9.89) * mm, "end": v(2.02, 9.49) * mm});
            skLineSegment(sketch, "E645", {"start": v(2.02, 9.49) * mm, "end": v(1.1, 9.03) * mm});
            skLineSegment(sketch, "E646", {"start": v(1.1, 9.03) * mm, "end": v(0.65, 8.65) * mm});
            skLineSegment(sketch, "E647", {"start": v(0.65, 8.65) * mm, "end": v(0.37, 8.16) * mm});
            skLineSegment(sketch, "E648", {"start": v(0.37, 8.16) * mm, "end": v(-0.3, 7.15) * mm});
            skLineSegment(sketch, "E649", {"start": v(-0.3, 7.15) * mm, "end": v(-0.5, 6.95) * mm});
            skLineSegment(sketch, "E650", {"start": v(-0.5, 6.95) * mm, "end": v(-0.43, 6.7) * mm});
            skLineSegment(sketch, "E651", {"start": v(-0.43, 6.7) * mm, "end": v(-0.26, 6.48) * mm});
            skLineSegment(sketch, "E652", {"start": v(-0.26, 6.48) * mm, "end": v(0, 6.23) * mm});
            skLineSegment(sketch, "E653", {"start": v(0, 6.23) * mm, "end": v(0.7, 5.35) * mm});
            skLineSegment(sketch, "E654", {"start": v(0.7, 5.35) * mm, "end": v(1.12, 5.08) * mm});
            skLineSegment(sketch, "E655", {"start": v(1.12, 5.08) * mm, "end": v(1.6, 4.93) * mm});
            skLineSegment(sketch, "E656", {"start": v(1.6, 4.93) * mm, "end": v(2.03, 4.92) * mm});
            skLineSegment(sketch, "E657", {"start": v(2.03, 4.92) * mm, "end": v(2.56, 5.04) * mm});
            skLineSegment(sketch, "E658", {"start": v(2.56, 5.04) * mm, "end": v(2.94, 5.3) * mm});
            skLineSegment(sketch, "E659", {"start": v(2.94, 5.3) * mm, "end": v(3.26, 5.57) * mm});
            skLineSegment(sketch, "E660", {"start": v(3.26, 5.57) * mm, "end": v(3.55, 6.37) * mm});
            skLineSegment(sketch, "E661", {"start": v(3.55, 6.37) * mm, "end": v(3.74, 7.3) * mm});
            skLineSegment(sketch, "E662", {"start": v(3.74, 7.3) * mm, "end": v(3.66, 7.55) * mm});
            skLineSegment(sketch, "E663", {"start": v(3.66, 7.55) * mm, "end": v(3.91, 7.34) * mm});
            skLineSegment(sketch, "E664", {"start": v(3.91, 7.34) * mm, "end": v(3.91, 7.18) * mm});
            skLineSegment(sketch, "E665", {"start": v(3.91, 7.18) * mm, "end": v(3.87, 6.9) * mm});
            skLineSegment(sketch, "E666", {"start": v(3.87, 6.9) * mm, "end": v(3.7, 6.16) * mm});
            skLineSegment(sketch, "E667", {"start": v(3.7, 6.16) * mm, "end": v(3.39, 5.42) * mm});
            skLineSegment(sketch, "E668", {"start": v(3.39, 5.42) * mm, "end": v(3.07, 4.74) * mm});
            skLineSegment(sketch, "E669", {"start": v(3.07, 4.74) * mm, "end": v(2.6, 4.38) * mm});
            skLineSegment(sketch, "E670", {"start": v(2.6, 4.38) * mm, "end": v(2.36, 4.2) * mm});
            skLineSegment(sketch, "E671", {"start": v(2.36, 4.2) * mm, "end": v(2.02, 4.08) * mm});
            skLineSegment(sketch, "E672", {"start": v(2.02, 4.08) * mm, "end": v(1.7, 4.07) * mm});
            skLineSegment(sketch, "E673", {"start": v(1.7, 4.07) * mm, "end": v(1.45, 4.07) * mm});
            skLineSegment(sketch, "E674", {"start": v(1.45, 4.07) * mm, "end": v(1.24, 4.07) * mm});
            skLineSegment(sketch, "E675", {"start": v(1.24, 4.07) * mm, "end": v(1.08, 4.14) * mm});
            skLineSegment(sketch, "E676", {"start": v(1.08, 4.14) * mm, "end": v(0.8, 4.2) * mm});
            skLineSegment(sketch, "E677", {"start": v(0.8, 4.2) * mm, "end": v(0.06, 4.5) * mm});
            skLineSegment(sketch, "E678", {"start": v(0.06, 4.5) * mm, "end": v(-0.53, 4.88) * mm});
            skLineSegment(sketch, "E679", {"start": v(-0.53, 4.88) * mm, "end": v(-1.15, 5.31) * mm});
            skLineSegment(sketch, "E680", {"start": v(-1.15, 5.31) * mm, "end": v(-1.38, 5.38) * mm});
            skLineSegment(sketch, "E681", {"start": v(-1.38, 5.38) * mm, "end": v(-1.53, 5.18) * mm});
            skLineSegment(sketch, "E682", {"start": v(-1.53, 5.18) * mm, "end": v(-1.97, 4.7) * mm});
            skLineSegment(sketch, "E683", {"start": v(-1.97, 4.7) * mm, "end": v(-2.46, 3.9) * mm});
            skLineSegment(sketch, "E684", {"start": v(-2.46, 3.9) * mm, "end": v(-3.9, 1.84) * mm});
            skLineSegment(sketch, "E685", {"start": v(-3.9, 1.84) * mm, "end": v(-4.47, 1.12) * mm});
            skLineSegment(sketch, "E686", {"start": v(-4.47, 1.12) * mm, "end": v(-4.88, 0.48) * mm});
            skLineSegment(sketch, "E687", {"start": v(-4.88, 0.48) * mm, "end": v(-5.27, -0.22) * mm});
            skLineSegment(sketch, "E688", {"start": v(-5.27, -0.22) * mm, "end": v(-5.6, -0.86) * mm});
            skLineSegment(sketch, "E689", {"start": v(-5.6, -0.86) * mm, "end": v(-5.75, -1.15) * mm});
            skLineSegment(sketch, "E690", {"start": v(-5.75, -1.15) * mm, "end": v(-6.08, -1.35) * mm});
            skLineSegment(sketch, "E691", {"start": v(-6.08, -1.35) * mm, "end": v(-6.65, -1.4) * mm});
            skLineSegment(sketch, "E692", {"start": v(-6.65, -1.4) * mm, "end": v(-7.28, -1.43) * mm});
            skLineSegment(sketch, "E693", {"start": v(-7.28, -1.43) * mm, "end": v(-7.58, -1.26) * mm});
            skLineSegment(sketch, "E694", {"start": v(-7.58, -1.26) * mm, "end": v(-7.9, -0.99) * mm});
            skLineSegment(sketch, "E695", {"start": v(-7.9, -0.99) * mm, "end": v(-7.88, -0.59) * mm});
            skLineSegment(sketch, "E696", {"start": v(-7.88, -0.59) * mm, "end": v(-7.75, -0.18) * mm});
            skLineSegment(sketch, "E697", {"start": v(-22.51, 29.11) * mm, "end": v(-22.62, 30.16) * mm});
            skLineSegment(sketch, "E698", {"start": v(-22.62, 30.16) * mm, "end": v(-22.52, 30.25) * mm});
            skLineSegment(sketch, "E699", {"start": v(-22.52, 30.25) * mm, "end": v(-22.33, 30.55) * mm});
            skLineSegment(sketch, "E700", {"start": v(-22.33, 30.55) * mm, "end": v(-21.96, 30.62) * mm});
            skLineSegment(sketch, "E701", {"start": v(-21.96, 30.62) * mm, "end": v(-21.54, 30.52) * mm});
            skLineSegment(sketch, "E702", {"start": v(-21.54, 30.52) * mm, "end": v(-21.37, 30.34) * mm});
            skLineSegment(sketch, "E703", {"start": v(-21.37, 30.34) * mm, "end": v(-21.24, 30.1) * mm});
            skLineSegment(sketch, "E704", {"start": v(-21.24, 30.1) * mm, "end": v(-21.28, 29.95) * mm});
            skLineSegment(sketch, "E705", {"start": v(-21.28, 29.95) * mm, "end": v(-21.33, 29.8) * mm});
            skLineSegment(sketch, "E706", {"start": v(-21.33, 29.8) * mm, "end": v(-21.46, 29.66) * mm});
            skLineSegment(sketch, "E707", {"start": v(-21.46, 29.66) * mm, "end": v(-21.68, 29.55) * mm});
            skLineSegment(sketch, "E708", {"start": v(-21.68, 29.55) * mm, "end": v(-21.88, 29.51) * mm});
            skLineSegment(sketch, "E709", {"start": v(-21.88, 29.51) * mm, "end": v(-22.1, 29.5) * mm});
            skLineSegment(sketch, "E710", {"start": v(-22.1, 29.5) * mm, "end": v(-22.18, 29.5) * mm});
            skLineSegment(sketch, "E711", {"start": v(-22.18, 29.5) * mm, "end": v(-22.2, 29.2) * mm});
            skLineSegment(sketch, "E712", {"start": v(-22.2, 29.2) * mm, "end": v(-22.27, 29.13) * mm});
            skLineSegment(sketch, "E713", {"start": v(-22.27, 29.13) * mm, "end": v(-22.51, 29.11) * mm});
            skLineSegment(sketch, "E714", {"start": v(-22.19, 29.79) * mm, "end": v(-22.17, 29.95) * mm});
            skLineSegment(sketch, "E715", {"start": v(-22.17, 29.95) * mm, "end": v(-22.08, 30.04) * mm});
            skLineSegment(sketch, "E716", {"start": v(-22.08, 30.04) * mm, "end": v(-22.05, 30.18) * mm});
            skLineSegment(sketch, "E717", {"start": v(-22.05, 30.18) * mm, "end": v(-22, 30.3) * mm});
            skLineSegment(sketch, "E718", {"start": v(-22, 30.3) * mm, "end": v(-21.66, 30.22) * mm});
            skLineSegment(sketch, "E719", {"start": v(-21.66, 30.22) * mm, "end": v(-21.63, 30.08) * mm});
            skLineSegment(sketch, "E720", {"start": v(-21.63, 30.08) * mm, "end": v(-21.66, 29.96) * mm});
            skLineSegment(sketch, "E721", {"start": v(-21.66, 29.96) * mm, "end": v(-21.73, 29.86) * mm});
            skLineSegment(sketch, "E722", {"start": v(-21.73, 29.86) * mm, "end": v(-21.85, 29.8) * mm});
            skLineSegment(sketch, "E723", {"start": v(-21.85, 29.8) * mm, "end": v(-22.19, 29.79) * mm});
            skLineSegment(sketch, "E724", {"start": v(-20.59, 30.6) * mm, "end": v(-20.59, 29.64) * mm});
            skLineSegment(sketch, "E725", {"start": v(-20.59, 29.64) * mm, "end": v(-20.49, 29.52) * mm});
            skLineSegment(sketch, "E726", {"start": v(-20.49, 29.52) * mm, "end": v(-20.29, 29.44) * mm});
            skLineSegment(sketch, "E727", {"start": v(-20.29, 29.44) * mm, "end": v(-20.05, 29.5) * mm});
            skLineSegment(sketch, "E728", {"start": v(-20.05, 29.5) * mm, "end": v(-19.92, 29.55) * mm});
            skLineSegment(sketch, "E729", {"start": v(-19.92, 29.55) * mm, "end": v(-19.89, 29.74) * mm});
            skLineSegment(sketch, "E730", {"start": v(-19.89, 29.74) * mm, "end": v(-19.9, 30.6) * mm});
            skLineSegment(sketch, "E731", {"start": v(-19.9, 30.6) * mm, "end": v(-19.48, 30.62) * mm});
            skLineSegment(sketch, "E732", {"start": v(-19.48, 30.62) * mm, "end": v(-19.47, 29.88) * mm});
            skLineSegment(sketch, "E733", {"start": v(-19.47, 29.88) * mm, "end": v(-19.55, 29.63) * mm});
            skLineSegment(sketch, "E734", {"start": v(-19.55, 29.63) * mm, "end": v(-19.55, 29.48) * mm});
            skLineSegment(sketch, "E735", {"start": v(-19.55, 29.48) * mm, "end": v(-19.67, 29.3) * mm});
            skLineSegment(sketch, "E736", {"start": v(-19.67, 29.3) * mm, "end": v(-19.87, 29.18) * mm});
            skLineSegment(sketch, "E737", {"start": v(-19.87, 29.18) * mm, "end": v(-20.34, 29.09) * mm});
            skLineSegment(sketch, "E738", {"start": v(-20.34, 29.09) * mm, "end": v(-20.48, 29.16) * mm});
            skLineSegment(sketch, "E739", {"start": v(-20.48, 29.16) * mm, "end": v(-20.65, 29.25) * mm});
            skLineSegment(sketch, "E740", {"start": v(-20.65, 29.25) * mm, "end": v(-20.86, 29.38) * mm});
            skLineSegment(sketch, "E741", {"start": v(-20.86, 29.38) * mm, "end": v(-20.85, 30.56) * mm});
            skLineSegment(sketch, "E742", {"start": v(-20.85, 30.56) * mm, "end": v(-20.59, 30.6) * mm});
            skLineSegment(sketch, "E743", {"start": v(-20.59, 30.6) * mm, "end": v(-20.59, 30.6) * mm});
            skLineSegment(sketch, "E744", {"start": v(-18.98, 29.1) * mm, "end": v(-18.99, 29.8) * mm});
            skLineSegment(sketch, "E745", {"start": v(-18.99, 29.8) * mm, "end": v(-18.78, 29.8) * mm});
            skLineSegment(sketch, "E746", {"start": v(-18.78, 29.8) * mm, "end": v(-18.65, 30) * mm});
            skLineSegment(sketch, "E747", {"start": v(-18.65, 30) * mm, "end": v(-18.74, 30.27) * mm});
            skLineSegment(sketch, "E748", {"start": v(-18.74, 30.27) * mm, "end": v(-18.91, 30.22) * mm});
            skLineSegment(sketch, "E749", {"start": v(-18.91, 30.22) * mm, "end": v(-19.02, 30.05) * mm});
            skLineSegment(sketch, "E750", {"start": v(-19.02, 30.05) * mm, "end": v(-19.08, 30) * mm});
            skLineSegment(sketch, "E751", {"start": v(-19.08, 30) * mm, "end": v(-19.1, 30.33) * mm});
            skLineSegment(sketch, "E752", {"start": v(-19.1, 30.33) * mm, "end": v(-18.83, 30.57) * mm});
            skLineSegment(sketch, "E753", {"start": v(-18.83, 30.57) * mm, "end": v(-18.48, 30.65) * mm});
            skLineSegment(sketch, "E754", {"start": v(-18.48, 30.65) * mm, "end": v(-18.18, 30.76) * mm});
            skLineSegment(sketch, "E755", {"start": v(-18.18, 30.76) * mm, "end": v(-18, 30.7) * mm});
            skLineSegment(sketch, "E756", {"start": v(-18, 30.7) * mm, "end": v(-17.58, 30.57) * mm});
            skLineSegment(sketch, "E757", {"start": v(-17.58, 30.57) * mm, "end": v(-17.39, 30.25) * mm});
            skLineSegment(sketch, "E758", {"start": v(-17.39, 30.25) * mm, "end": v(-17.62, 29.91) * mm});
            skLineSegment(sketch, "E759", {"start": v(-17.62, 29.91) * mm, "end": v(-17.5, 29.82) * mm});
            skLineSegment(sketch, "E760", {"start": v(-17.5, 29.82) * mm, "end": v(-17.46, 29.7) * mm});
            skLineSegment(sketch, "E761", {"start": v(-17.46, 29.7) * mm, "end": v(-17.45, 29.39) * mm});
            skLineSegment(sketch, "E762", {"start": v(-17.45, 29.39) * mm, "end": v(-17.45, 29.26) * mm});
            skLineSegment(sketch, "E763", {"start": v(-17.45, 29.26) * mm, "end": v(-17.46, 29.22) * mm});
            skLineSegment(sketch, "E764", {"start": v(-17.46, 29.22) * mm, "end": v(-17.9, 29.23) * mm});
            skLineSegment(sketch, "E765", {"start": v(-17.9, 29.23) * mm, "end": v(-17.91, 29.63) * mm});
            skLineSegment(sketch, "E766", {"start": v(-17.91, 29.63) * mm, "end": v(-18.03, 29.7) * mm});
            skLineSegment(sketch, "E767", {"start": v(-18.03, 29.7) * mm, "end": v(-18.1, 29.67) * mm});
            skLineSegment(sketch, "E768", {"start": v(-18.1, 29.67) * mm, "end": v(-18.15, 29.42) * mm});
            skLineSegment(sketch, "E769", {"start": v(-18.15, 29.42) * mm, "end": v(-18.93, 28.96) * mm});
            skLineSegment(sketch, "E770", {"start": v(-18.93, 28.96) * mm, "end": v(-19.14, 28.95) * mm});
            skLineSegment(sketch, "E771", {"start": v(-19.14, 28.95) * mm, "end": v(-19.14, 29.04) * mm});
            skLineSegment(sketch, "E772", {"start": v(-19.14, 29.04) * mm, "end": v(-18.97, 29.1) * mm});
            skLineSegment(sketch, "E773", {"start": v(-18.25, 30.2) * mm, "end": v(-18.15, 30.07) * mm});
            skLineSegment(sketch, "E774", {"start": v(-18.15, 30.07) * mm, "end": v(-18.02, 30.07) * mm});
            skLineSegment(sketch, "E775", {"start": v(-18.02, 30.07) * mm, "end": v(-17.91, 30.1) * mm});
            skLineSegment(sketch, "E776", {"start": v(-17.91, 30.1) * mm, "end": v(-17.9, 30.17) * mm});
            skLineSegment(sketch, "E777", {"start": v(-17.9, 30.17) * mm, "end": v(-17.92, 30.23) * mm});
            skLineSegment(sketch, "E778", {"start": v(-17.92, 30.23) * mm, "end": v(-18.02, 30.31) * mm});
            skLineSegment(sketch, "E779", {"start": v(-18.02, 30.31) * mm, "end": v(-18.24, 30.3) * mm});
            skLineSegment(sketch, "E780", {"start": v(-18.24, 30.3) * mm, "end": v(-18.29, 30.26) * mm});
            skLineSegment(sketch, "E781", {"start": v(-18.29, 30.26) * mm, "end": v(-18.25, 30.2) * mm});
            skLineSegment(sketch, "E782", {"start": v(-15.41, 30.73) * mm, "end": v(-15.41, 30.45) * mm});
            skLineSegment(sketch, "E783", {"start": v(-15.41, 30.45) * mm, "end": v(-16.25, 30.45) * mm});
            skLineSegment(sketch, "E784", {"start": v(-16.25, 30.45) * mm, "end": v(-16.4, 30.38) * mm});
            skLineSegment(sketch, "E785", {"start": v(-16.4, 30.38) * mm, "end": v(-16.5, 30.27) * mm});
            skLineSegment(sketch, "E786", {"start": v(-16.5, 30.27) * mm, "end": v(-16.47, 30.15) * mm});
            skLineSegment(sketch, "E787", {"start": v(-16.47, 30.15) * mm, "end": v(-16.3, 30.1) * mm});
            skLineSegment(sketch, "E788", {"start": v(-16.3, 30.1) * mm, "end": v(-16.08, 30.12) * mm});
            skLineSegment(sketch, "E789", {"start": v(-16.08, 30.12) * mm, "end": v(-15.57, 30.13) * mm});
            skLineSegment(sketch, "E790", {"start": v(-15.57, 30.13) * mm, "end": v(-15.56, 29.89) * mm});
            skLineSegment(sketch, "E791", {"start": v(-15.56, 29.89) * mm, "end": v(-16.44, 29.87) * mm});
            skLineSegment(sketch, "E792", {"start": v(-16.44, 29.87) * mm, "end": v(-16.5, 29.75) * mm});
            skLineSegment(sketch, "E793", {"start": v(-16.5, 29.75) * mm, "end": v(-16.4, 29.57) * mm});
            skLineSegment(sketch, "E794", {"start": v(-16.4, 29.57) * mm, "end": v(-15.5, 29.57) * mm});
            skLineSegment(sketch, "E795", {"start": v(-15.5, 29.57) * mm, "end": v(-15.38, 29.57) * mm});
            skLineSegment(sketch, "E796", {"start": v(-15.38, 29.57) * mm, "end": v(-15.38, 29.29) * mm});
            skLineSegment(sketch, "E797", {"start": v(-15.38, 29.29) * mm, "end": v(-16.57, 29.29) * mm});
            skLineSegment(sketch, "E798", {"start": v(-16.57, 29.29) * mm, "end": v(-16.8, 29.38) * mm});
            skLineSegment(sketch, "E799", {"start": v(-16.8, 29.38) * mm, "end": v(-16.88, 29.53) * mm});
            skLineSegment(sketch, "E800", {"start": v(-16.88, 29.53) * mm, "end": v(-16.92, 29.64) * mm});
            skLineSegment(sketch, "E801", {"start": v(-16.92, 29.64) * mm, "end": v(-16.93, 29.83) * mm});
            skLineSegment(sketch, "E802", {"start": v(-16.93, 29.83) * mm, "end": v(-16.92, 30.05) * mm});
            skLineSegment(sketch, "E803", {"start": v(-16.92, 30.05) * mm, "end": v(-16.87, 30.28) * mm});
            skLineSegment(sketch, "E804", {"start": v(-16.87, 30.28) * mm, "end": v(-16.83, 30.54) * mm});
            skLineSegment(sketch, "E805", {"start": v(-16.83, 30.54) * mm, "end": v(-16.7, 30.6) * mm});
            skLineSegment(sketch, "E806", {"start": v(-16.7, 30.6) * mm, "end": v(-16.62, 30.66) * mm});
            skLineSegment(sketch, "E807", {"start": v(-16.62, 30.66) * mm, "end": v(-16.18, 30.7) * mm});
            skLineSegment(sketch, "E808", {"start": v(-16.18, 30.7) * mm, "end": v(-15.41, 30.73) * mm});
            skLineSegment(sketch, "E809", {"start": v(-21.5, 31.56) * mm, "end": v(-21.51, 32.04) * mm});
            skLineSegment(sketch, "E810", {"start": v(-21.51, 32.04) * mm, "end": v(-21.3, 32.17) * mm});
            skLineSegment(sketch, "E811", {"start": v(-21.3, 32.17) * mm, "end": v(-21.18, 32.14) * mm});
            skLineSegment(sketch, "E812", {"start": v(-21.18, 32.14) * mm, "end": v(-21.06, 32.02) * mm});
            skLineSegment(sketch, "E813", {"start": v(-21.06, 32.02) * mm, "end": v(-21.07, 31.53) * mm});
            skLineSegment(sketch, "E814", {"start": v(-21.07, 31.53) * mm, "end": v(-21.19, 31.51) * mm});
            skLineSegment(sketch, "E815", {"start": v(-21.19, 31.51) * mm, "end": v(-21.2, 31.9) * mm});
            skLineSegment(sketch, "E816", {"start": v(-21.2, 31.9) * mm, "end": v(-21.3, 31.99) * mm});
            skLineSegment(sketch, "E817", {"start": v(-21.3, 31.99) * mm, "end": v(-21.33, 31.92) * mm});
            skLineSegment(sketch, "E818", {"start": v(-21.33, 31.92) * mm, "end": v(-21.32, 31.5) * mm});
            skLineSegment(sketch, "E819", {"start": v(-21.32, 31.5) * mm, "end": v(-21.5, 31.56) * mm});
            skLineSegment(sketch, "E820", {"start": v(-20.85, 31.77) * mm, "end": v(-20.74, 31.56) * mm});
            skLineSegment(sketch, "E821", {"start": v(-20.74, 31.56) * mm, "end": v(-20.6, 31.47) * mm});
            skLineSegment(sketch, "E822", {"start": v(-20.6, 31.47) * mm, "end": v(-20.45, 31.5) * mm});
            skLineSegment(sketch, "E823", {"start": v(-20.45, 31.5) * mm, "end": v(-20.39, 31.53) * mm});
            skLineSegment(sketch, "E824", {"start": v(-20.39, 31.53) * mm, "end": v(-20.32, 31.5) * mm});
            skLineSegment(sketch, "E825", {"start": v(-20.32, 31.5) * mm, "end": v(-20.28, 31.97) * mm});
            skLineSegment(sketch, "E826", {"start": v(-20.28, 31.97) * mm, "end": v(-20.37, 32.14) * mm});
            skLineSegment(sketch, "E827", {"start": v(-20.37, 32.14) * mm, "end": v(-20.54, 32.2) * mm});
            skLineSegment(sketch, "E828", {"start": v(-20.54, 32.2) * mm, "end": v(-20.73, 32.1) * mm});
            skLineSegment(sketch, "E829", {"start": v(-20.73, 32.1) * mm, "end": v(-20.79, 31.89) * mm});
            skLineSegment(sketch, "E830", {"start": v(-20.79, 31.89) * mm, "end": v(-20.85, 31.76) * mm});
            skLineSegment(sketch, "E831", {"start": v(-20.64, 31.8) * mm, "end": v(-20.56, 31.74) * mm});
            skLineSegment(sketch, "E832", {"start": v(-20.56, 31.74) * mm, "end": v(-20.49, 31.75) * mm});
            skLineSegment(sketch, "E833", {"start": v(-20.49, 31.75) * mm, "end": v(-20.45, 31.79) * mm});
            skLineSegment(sketch, "E834", {"start": v(-20.45, 31.79) * mm, "end": v(-20.45, 31.89) * mm});
            skLineSegment(sketch, "E835", {"start": v(-20.45, 31.89) * mm, "end": v(-20.51, 31.94) * mm});
            skLineSegment(sketch, "E836", {"start": v(-20.51, 31.94) * mm, "end": v(-20.63, 31.95) * mm});
            skLineSegment(sketch, "E837", {"start": v(-20.63, 31.95) * mm, "end": v(-20.66, 31.91) * mm});
            skLineSegment(sketch, "E838", {"start": v(-20.66, 31.91) * mm, "end": v(-20.66, 31.84) * mm});
            skLineSegment(sketch, "E839", {"start": v(-20.66, 31.84) * mm, "end": v(-20.64, 31.8) * mm});
            skLineSegment(sketch, "E840", {"start": v(-20.04, 32.13) * mm, "end": v(-20.04, 31.83) * mm});
            skLineSegment(sketch, "E841", {"start": v(-20.04, 31.83) * mm, "end": v(-19.92, 31.59) * mm});
            skLineSegment(sketch, "E842", {"start": v(-19.92, 31.59) * mm, "end": v(-19.85, 31.54) * mm});
            skLineSegment(sketch, "E843", {"start": v(-19.85, 31.54) * mm, "end": v(-19.75, 31.57) * mm});
            skLineSegment(sketch, "E844", {"start": v(-19.75, 31.57) * mm, "end": v(-19.72, 31.65) * mm});
            skLineSegment(sketch, "E845", {"start": v(-19.72, 31.65) * mm, "end": v(-19.74, 31.8) * mm});
            skLineSegment(sketch, "E846", {"start": v(-19.74, 31.8) * mm, "end": v(-19.9, 31.92) * mm});
            skLineSegment(sketch, "E847", {"start": v(-19.9, 31.92) * mm, "end": v(-19.83, 32) * mm});
            skLineSegment(sketch, "E848", {"start": v(-19.83, 32) * mm, "end": v(-19.73, 32.04) * mm});
            skLineSegment(sketch, "E849", {"start": v(-19.73, 32.04) * mm, "end": v(-19.7, 32.23) * mm});
            skLineSegment(sketch, "E850", {"start": v(-19.7, 32.23) * mm, "end": v(-19.85, 32.26) * mm});
            skLineSegment(sketch, "E851", {"start": v(-19.85, 32.26) * mm, "end": v(-19.87, 32.35) * mm});
            skLineSegment(sketch, "E852", {"start": v(-19.87, 32.35) * mm, "end": v(-19.98, 32.39) * mm});
            skLineSegment(sketch, "E853", {"start": v(-19.98, 32.39) * mm, "end": v(-20.03, 32.3) * mm});
            skLineSegment(sketch, "E854", {"start": v(-20.03, 32.3) * mm, "end": v(-20.04, 32.13) * mm});
            skLineSegment(sketch, "E855", {"start": v(-19.48, 32.22) * mm, "end": v(-19.48, 31.77) * mm});
            skLineSegment(sketch, "E856", {"start": v(-19.48, 31.77) * mm, "end": v(-19.43, 31.66) * mm});
            skLineSegment(sketch, "E857", {"start": v(-19.43, 31.66) * mm, "end": v(-19.35, 31.56) * mm});
            skLineSegment(sketch, "E858", {"start": v(-19.35, 31.56) * mm, "end": v(-19.27, 31.55) * mm});
            skLineSegment(sketch, "E859", {"start": v(-19.27, 31.55) * mm, "end": v(-19.18, 31.55) * mm});
            skLineSegment(sketch, "E860", {"start": v(-19.18, 31.55) * mm, "end": v(-19.09, 31.62) * mm});
            skLineSegment(sketch, "E861", {"start": v(-19.09, 31.62) * mm, "end": v(-19.04, 31.69) * mm});
            skLineSegment(sketch, "E862", {"start": v(-19.04, 31.69) * mm, "end": v(-18.98, 31.82) * mm});
            skLineSegment(sketch, "E863", {"start": v(-18.98, 31.82) * mm, "end": v(-18.98, 31.95) * mm});
            skLineSegment(sketch, "E864", {"start": v(-18.98, 31.95) * mm, "end": v(-18.98, 32.17) * mm});
            skLineSegment(sketch, "E865", {"start": v(-18.98, 32.17) * mm, "end": v(-19, 32.27) * mm});
            skLineSegment(sketch, "E866", {"start": v(-19, 32.27) * mm, "end": v(-19.18, 32.25) * mm});
            skLineSegment(sketch, "E867", {"start": v(-19.18, 32.25) * mm, "end": v(-19.18, 31.9) * mm});
            skLineSegment(sketch, "E868", {"start": v(-19.18, 31.9) * mm, "end": v(-19.21, 31.8) * mm});
            skLineSegment(sketch, "E869", {"start": v(-19.21, 31.8) * mm, "end": v(-19.3, 31.79) * mm});
            skLineSegment(sketch, "E870", {"start": v(-19.3, 31.79) * mm, "end": v(-19.33, 31.88) * mm});
            skLineSegment(sketch, "E871", {"start": v(-19.33, 31.88) * mm, "end": v(-19.33, 32.04) * mm});
            skLineSegment(sketch, "E872", {"start": v(-19.33, 32.04) * mm, "end": v(-19.33, 32.18) * mm});
            skLineSegment(sketch, "E873", {"start": v(-19.33, 32.18) * mm, "end": v(-19.34, 32.25) * mm});
            skLineSegment(sketch, "E874", {"start": v(-19.34, 32.25) * mm, "end": v(-19.48, 32.22) * mm});
            skLineSegment(sketch, "E875", {"start": v(-18.71, 31.6) * mm, "end": v(-18.71, 32.1) * mm});
            skLineSegment(sketch, "E876", {"start": v(-18.71, 32.1) * mm, "end": v(-18.6, 32.21) * mm});
            skLineSegment(sketch, "E877", {"start": v(-18.6, 32.21) * mm, "end": v(-18.52, 32.2) * mm});
            skLineSegment(sketch, "E878", {"start": v(-18.52, 32.2) * mm, "end": v(-18.47, 32.08) * mm});
            skLineSegment(sketch, "E879", {"start": v(-18.47, 32.08) * mm, "end": v(-18.43, 31.99) * mm});
            skLineSegment(sketch, "E880", {"start": v(-18.43, 31.99) * mm, "end": v(-18.49, 31.9) * mm});
            skLineSegment(sketch, "E881", {"start": v(-18.49, 31.9) * mm, "end": v(-18.57, 31.9) * mm});
            skLineSegment(sketch, "E882", {"start": v(-18.57, 31.9) * mm, "end": v(-18.53, 31.68) * mm});
            skLineSegment(sketch, "E883", {"start": v(-18.53, 31.68) * mm, "end": v(-18.5, 31.57) * mm});
            skLineSegment(sketch, "E884", {"start": v(-18.5, 31.57) * mm, "end": v(-18.71, 31.6) * mm});
            skLineSegment(sketch, "E885", {"start": v(-18.13, 31.86) * mm, "end": v(-18, 31.66) * mm});
            skLineSegment(sketch, "E886", {"start": v(-18, 31.66) * mm, "end": v(-17.92, 31.6) * mm});
            skLineSegment(sketch, "E887", {"start": v(-17.92, 31.6) * mm, "end": v(-17.6, 31.62) * mm});
            skLineSegment(sketch, "E888", {"start": v(-17.6, 31.62) * mm, "end": v(-17.55, 31.62) * mm});
            skLineSegment(sketch, "E889", {"start": v(-17.55, 31.62) * mm, "end": v(-17.55, 31.73) * mm});
            skLineSegment(sketch, "E890", {"start": v(-17.55, 31.73) * mm, "end": v(-17.59, 31.73) * mm});
            skLineSegment(sketch, "E891", {"start": v(-17.59, 31.73) * mm, "end": v(-17.54, 31.92) * mm});
            skLineSegment(sketch, "E892", {"start": v(-17.54, 31.92) * mm, "end": v(-17.53, 32.04) * mm});
            skLineSegment(sketch, "E893", {"start": v(-17.53, 32.04) * mm, "end": v(-17.71, 32.3) * mm});
            skLineSegment(sketch, "E894", {"start": v(-17.71, 32.3) * mm, "end": v(-17.9, 32.34) * mm});
            skLineSegment(sketch, "E895", {"start": v(-17.9, 32.34) * mm, "end": v(-18, 32.17) * mm});
            skLineSegment(sketch, "E896", {"start": v(-18, 32.17) * mm, "end": v(-18.1, 32.04) * mm});
            skLineSegment(sketch, "E897", {"start": v(-18.1, 32.04) * mm, "end": v(-18.13, 31.86) * mm});
            skLineSegment(sketch, "E898", {"start": v(-17.94, 31.96) * mm, "end": v(-17.94, 31.86) * mm});
            skLineSegment(sketch, "E899", {"start": v(-17.94, 31.86) * mm, "end": v(-17.91, 31.77) * mm});
            skLineSegment(sketch, "E900", {"start": v(-17.91, 31.77) * mm, "end": v(-17.75, 31.75) * mm});
            skLineSegment(sketch, "E901", {"start": v(-17.75, 31.75) * mm, "end": v(-17.7, 31.8) * mm});
            skLineSegment(sketch, "E902", {"start": v(-17.7, 31.8) * mm, "end": v(-17.67, 31.89) * mm});
            skLineSegment(sketch, "E903", {"start": v(-17.67, 31.89) * mm, "end": v(-17.7, 31.98) * mm});
            skLineSegment(sketch, "E904", {"start": v(-17.7, 31.98) * mm, "end": v(-17.78, 32.03) * mm});
            skLineSegment(sketch, "E905", {"start": v(-17.78, 32.03) * mm, "end": v(-17.87, 32.04) * mm});
            skLineSegment(sketch, "E906", {"start": v(-17.87, 32.04) * mm, "end": v(-17.94, 31.96) * mm});
            skLineSegment(sketch, "E907", {"start": v(-17.2, 32.61) * mm, "end": v(-16.99, 32.61) * mm});
            skLineSegment(sketch, "E908", {"start": v(-16.99, 32.61) * mm, "end": v(-16.98, 31.94) * mm});
            skLineSegment(sketch, "E909", {"start": v(-16.98, 31.94) * mm, "end": v(-16.87, 31.78) * mm});
            skLineSegment(sketch, "E910", {"start": v(-16.87, 31.78) * mm, "end": v(-16.87, 31.6) * mm});
            skLineSegment(sketch, "E911", {"start": v(-16.87, 31.6) * mm, "end": v(-17.02, 31.6) * mm});
            skLineSegment(sketch, "E912", {"start": v(-17.02, 31.6) * mm, "end": v(-17.04, 31.67) * mm});
            skLineSegment(sketch, "E913", {"start": v(-17.04, 31.67) * mm, "end": v(-17.12, 31.75) * mm});
            skLineSegment(sketch, "E914", {"start": v(-17.12, 31.75) * mm, "end": v(-17.2, 31.96) * mm});
            skLineSegment(sketch, "E915", {"start": v(-17.2, 31.96) * mm, "end": v(-17.16, 32.61) * mm});
            skText(sketch, "E916", { "text": "Pryce", "fontName": "OpenSans-Regular.ttf"});
            skLineSegment(sketch, "E917", {"start": v(-23.54, 39.42) * mm, "end": v(2.37, 39.42) * mm, "construction": true});
            skCircle(sketch, "E918", {"center": v(-10.58, 39.42) * mm, "radius": 1.81 * mm});
            const initialGuessF0  = {"E916": [-0.01845, -0.01132, 1, 0, 0.00453]};
            skSetInitialGuess(sketch, initialGuessF0);
            skSolve(sketch);
        }
        {
            var Q0;
            Q0=makeQuery(id+"F0.imprint","IMPRINT",FACE,{"disambiguationData":[TD([[makeQuery(id+"F0.imprint","IMPRINT",EDGE,{"derivedFrom":sQuery(id+"F0.wireOp",EDGE,"E916.sketch_text.stroke-59")}),-1.0]])]});
            var Q1;
            Q1=makeQuery(id+"F0.imprint","IMPRINT",FACE,{"disambiguationData":[TD([[makeQuery(id+"F0.imprint","IMPRINT",EDGE,{"derivedFrom":sQuery(id+"F0.wireOp",EDGE,"E916.sketch_text.stroke-44")}),-1.0]])]});
            var Q2;
            Q2=makeQuery(id+"F0.imprint","IMPRINT",FACE,{"disambiguationData":[TD([[makeQuery(id+"F0.imprint","IMPRINT",EDGE,{"derivedFrom":sQuery(id+"F0.wireOp",EDGE,"E916.sketch_text.stroke-28")}),-1.0]])]});
            var Q3;
            Q3=makeQuery(id+"F0.imprint","IMPRINT",FACE,{"disambiguationData":[TD([[makeQuery(id+"F0.imprint","IMPRINT",EDGE,{"derivedFrom":sQuery(id+"F0.wireOp",EDGE,"E916.sketch_text.stroke-15")}),-1.0]])]});
            var Q4;
            Q4=makeQuery(id+"F0.imprint","IMPRINT",FACE,{"disambiguationData":[TD([[makeQuery(id+"F0.imprint","IMPRINT",EDGE,{"derivedFrom":sQuery(id+"F0.wireOp",EDGE,"E916.sketch_text.stroke-0")}),-1.0]])]});
            var Q5;
            Q5=makeQuery(id+"F0.imprint","IMPRINT",FACE,{"disambiguationData":[TD([[makeQuery(id+"F0.imprint","IMPRINT",EDGE,{"derivedFrom":sQuery(id+"F0.wireOp",EDGE,"E486")}),1.0]])]});
            var Q6;
            Q6=makeQuery(id+"F0.imprint","IMPRINT",FACE,{"disambiguationData":[TD([[makeQuery(id+"F0.imprint","IMPRINT",EDGE,{"derivedFrom":sQuery(id+"F0.wireOp",EDGE,"E419")}),-1.0]])]});
            var Q7;
            Q7=makeQuery(id+"F0.imprint","IMPRINT",FACE,{"disambiguationData":[TD([[makeQuery(id+"F0.imprint","IMPRINT",EDGE,{"derivedFrom":sQuery(id+"F0.wireOp",EDGE,"E296")}),1.0]])]});
            var Q8;
            Q8=makeQuery(id+"F0.imprint","IMPRINT",FACE,{"disambiguationData":[TD([[makeQuery(id+"F0.imprint","IMPRINT",EDGE,{"derivedFrom":sQuery(id+"F0.wireOp",EDGE,"E551")}),-1.0]])]});
            var Q9;
            Q9=makeQuery(id+"F0.imprint","IMPRINT",FACE,{"disambiguationData":[TD([[makeQuery(id+"F0.imprint","IMPRINT",EDGE,{"derivedFrom":sQuery(id+"F0.wireOp",EDGE,"E607")}),-1.0]])]});
            var Q10;
            Q10=makeQuery(id+"F0.imprint","IMPRINT",FACE,{"disambiguationData":[TD([[makeQuery(id+"F0.imprint","IMPRINT",EDGE,{"derivedFrom":sQuery(id+"F0.wireOp",EDGE,"E78")}),-1.0]])]});
            var Q11;
            Q11=makeQuery(id+"F0.imprint","IMPRINT",FACE,{"disambiguationData":[TD([[makeQuery(id+"F0.imprint","IMPRINT",EDGE,{"derivedFrom":sQuery(id+"F0.wireOp",EDGE,"E224")}),1.0]])]});
            extrude(context, id + "F1", {"entities" : qUnion([Q0, Q1, Q2, Q3, Q4, Q5, Q6, Q7, Q8, Q9, Q10, Q11]), "depth" : 2.54 * mm, "offsetDistance" : 25.4 * mm});
        }
        {
            var Q0;
            Q0=makeQuery(id+"F0.imprint","IMPRINT",FACE,{"disambiguationData":[TD([[makeQuery(id+"F0.imprint","IMPRINT",EDGE,{"derivedFrom":sQuery(id+"F0.wireOp",EDGE,"E0")}),1.0]])]});
            extrude(context, id + "F2", {"entities" : qUnion([Q0]), "depth" : 5.08 * mm, "offsetDistance" : 25.4 * mm});
        }
    });
